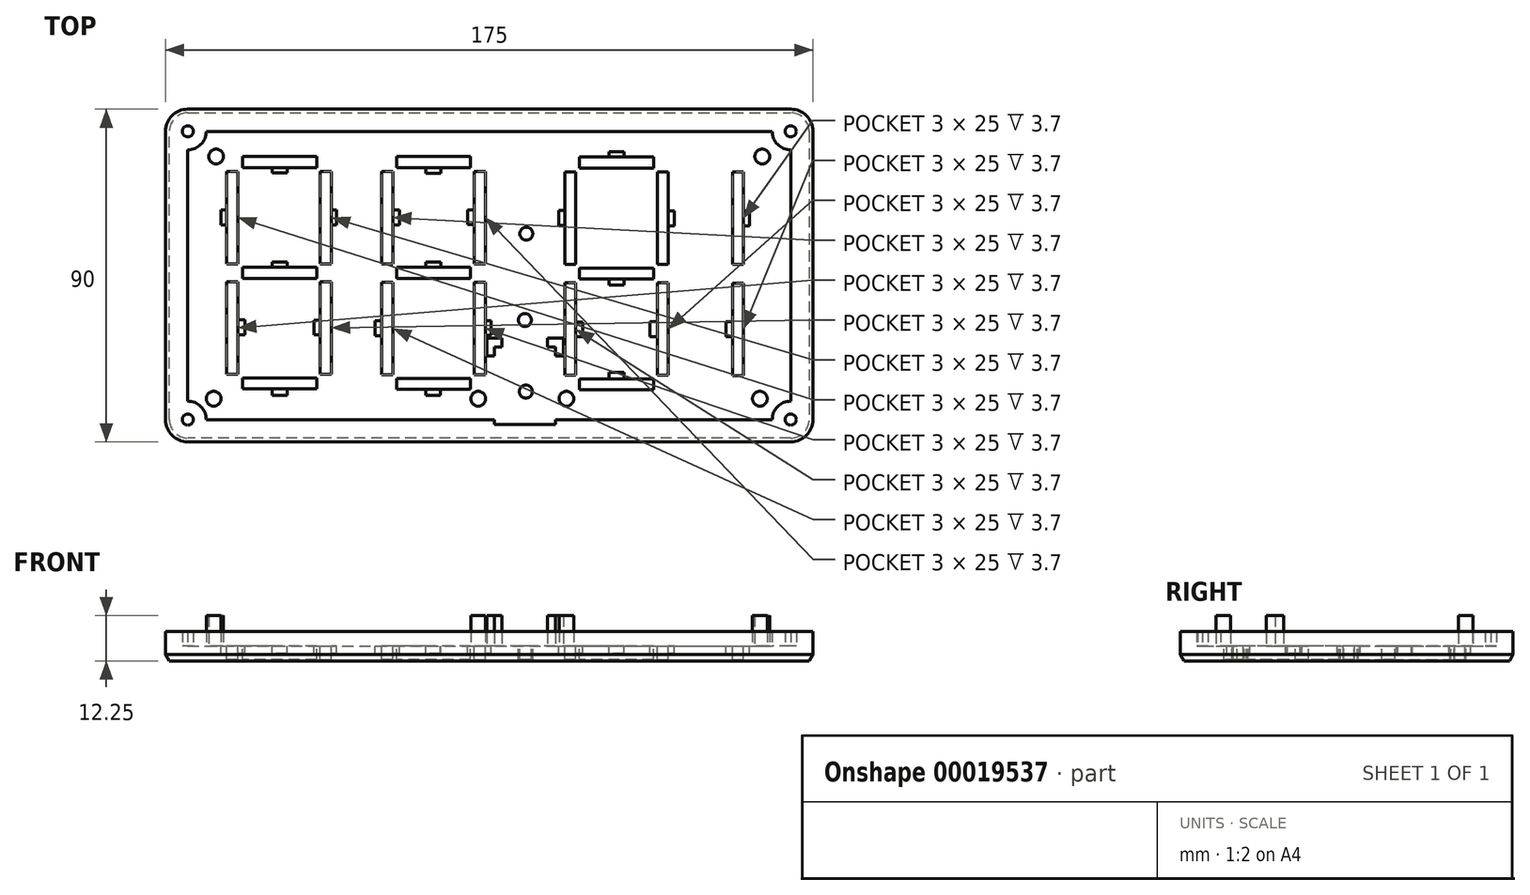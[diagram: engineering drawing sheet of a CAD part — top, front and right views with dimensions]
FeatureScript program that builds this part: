
annotation { "Feature Type Name" : "Feature", "Feature Type Description" : "" }
export const myFeature = defineFeature(function(context is Context, id is Id, definition is map)
    precondition{}
    {
        {
            var Q0;
            Q0=qCreatedBy(makeId("Top.planeOp"),FACE);
            var sketch = newSketch(context, id + "F0", { "sketchPlane" : qUnion([Q0])});
            skLineSegment(sketch, "E0.bottom", {"start": v(-87.5, 45) * mm, "end": v(87.5, 45) * mm});
            skLineSegment(sketch, "E0.top", {"start": v(-87.5, -45) * mm, "end": v(87.5, -45) * mm});
            skLineSegment(sketch, "E0.left", {"start": v(-87.5, 45) * mm, "end": v(-87.5, -45) * mm});
            skLineSegment(sketch, "E0.right", {"start": v(87.5, 45) * mm, "end": v(87.5, -45) * mm});
            skArc(sketch, "E1", {"start": v(-81.5, 34) * mm, "mid": v(-77.96, 35.46) * mm, "end": v(-76.5, 39) * mm});
            skArc(sketch, "E2", {"start": v(76.5, 39) * mm, "mid": v(77.96, 35.46) * mm, "end": v(81.5, 34) * mm});
            skArc(sketch, "E3", {"start": v(-76.5, -39) * mm, "mid": v(-77.96, -35.46) * mm, "end": v(-81.5, -34) * mm});
            skArc(sketch, "E4", {"start": v(81.5, -34) * mm, "mid": v(77.96, -35.46) * mm, "end": v(76.5, -39) * mm});
            skLineSegment(sketch, "E5", {"start": v(0, 39) * mm, "end": v(0, 0) * mm, "construction": true});
            skLineSegment(sketch, "E6.top", {"start": v(-68.01, -26.67) * mm, "end": v(-71.01, -26.67) * mm});
            skLineSegment(sketch, "E6.left", {"start": v(-68.01, -1.67) * mm, "end": v(-68.01, -26.67) * mm});
            skLineSegment(sketch, "E7.left", {"start": v(-68.01, 3.19) * mm, "end": v(-68.01, 28.19) * mm});
            skLineSegment(sketch, "E6.right", {"start": v(-71.01, -1.67) * mm, "end": v(-71.01, -26.67) * mm});
            skLineSegment(sketch, "E7.right", {"start": v(-71.01, 3.19) * mm, "end": v(-71.01, 28.19) * mm});
            skLineSegment(sketch, "E8.bottom", {"start": v(-45.68, -1.67) * mm, "end": v(-42.68, -1.67) * mm});
            skLineSegment(sketch, "E8.top", {"start": v(-45.68, -26.67) * mm, "end": v(-42.68, -26.67) * mm});
            skLineSegment(sketch, "E9.left", {"start": v(-46.68, 2.19) * mm, "end": v(-46.68, 29.19) * mm, "construction": true});
            skLineSegment(sketch, "E8.left", {"start": v(-45.68, -1.67) * mm, "end": v(-45.68, -26.67) * mm});
            skLineSegment(sketch, "E8.right", {"start": v(-42.68, -1.67) * mm, "end": v(-42.68, -26.67) * mm});
            skLineSegment(sketch, "E9.right", {"start": v(-41.68, 2.19) * mm, "end": v(-41.68, 29.19) * mm, "construction": true});
            skLineSegment(sketch, "E10", {"start": v(-45.68, -26.67) * mm, "end": v(-68.01, -26.67) * mm, "construction": true});
            skLineSegment(sketch, "E11.bottom", {"start": v(-46.68, -27.67) * mm, "end": v(-66.68, -27.67) * mm});
            skLineSegment(sketch, "E11.top", {"start": v(-46.68, -30.67) * mm, "end": v(-66.68, -30.67) * mm});
            skLineSegment(sketch, "E12.left", {"start": v(-66.68, 2.19) * mm, "end": v(-66.68, 29.19) * mm, "construction": true});
            skLineSegment(sketch, "E12.right", {"start": v(-72.01, 2.19) * mm, "end": v(-72.01, 29.19) * mm, "construction": true});
            skLineSegment(sketch, "E13.bottom", {"start": v(-46.68, 29.19) * mm, "end": v(-66.68, 29.19) * mm});
            skLineSegment(sketch, "E13.top", {"start": v(-46.68, 32.19) * mm, "end": v(-66.68, 32.19) * mm});
            skLineSegment(sketch, "E14.right", {"start": v(-42.68, 3.19) * mm, "end": v(-42.68, 28.19) * mm});
            skLineSegment(sketch, "E15.rect.bottom", {"start": v(-46.68, 2.19) * mm, "end": v(-66.68, 2.19) * mm});
            skLineSegment(sketch, "E15.rect.top", {"start": v(-46.68, -0.81) * mm, "end": v(-66.68, -0.81) * mm});
            skLineSegment(sketch, "E16.rect.bottom", {"start": v(-45.68, 3.19) * mm, "end": v(-68.01, 3.19) * mm, "construction": true});
            skLineSegment(sketch, "E16.rect.top", {"start": v(-45.68, -1.67) * mm, "end": v(-68.01, -1.67) * mm, "construction": true});
            skLineSegment(sketch, "E14.bottom", {"start": v(-45.68, 3.19) * mm, "end": v(-42.68, 3.19) * mm});
            skLineSegment(sketch, "E14.left", {"start": v(-45.68, 3.19) * mm, "end": v(-45.68, 28.19) * mm});
            skLineSegment(sketch, "E9.top", {"start": v(-46.68, 29.19) * mm, "end": v(-41.68, 29.19) * mm, "construction": true});
            skLineSegment(sketch, "E12.bottom", {"start": v(-66.68, 2.19) * mm, "end": v(-72.01, 2.19) * mm, "construction": true});
            skLineSegment(sketch, "E12.top", {"start": v(-66.68, 29.19) * mm, "end": v(-72.01, 29.19) * mm, "construction": true});
            skLineSegment(sketch, "E11.left", {"start": v(-46.68, -27.67) * mm, "end": v(-46.68, -30.67) * mm});
            skLineSegment(sketch, "E11.right", {"start": v(-66.68, -27.67) * mm, "end": v(-66.68, -30.67) * mm});
            skLineSegment(sketch, "E13.right", {"start": v(-66.68, 29.19) * mm, "end": v(-66.68, 32.19) * mm});
            skLineSegment(sketch, "E7.bottom", {"start": v(-68.01, 3.19) * mm, "end": v(-71.01, 3.19) * mm});
            skLineSegment(sketch, "E7.top", {"start": v(-68.01, 28.19) * mm, "end": v(-71.01, 28.19) * mm});
            skLineSegment(sketch, "E15.rect.left", {"start": v(-46.68, 2.19) * mm, "end": v(-46.68, -0.81) * mm});
            skLineSegment(sketch, "E15.rect.right", {"start": v(-66.68, 2.19) * mm, "end": v(-66.68, -0.81) * mm});
            skLineSegment(sketch, "E16.rect.right", {"start": v(-68.01, 3.19) * mm, "end": v(-68.01, -1.67) * mm, "construction": true});
            skLineSegment(sketch, "E13.left", {"start": v(-46.68, 29.19) * mm, "end": v(-46.68, 32.19) * mm});
            skLineSegment(sketch, "E14.top", {"start": v(-45.68, 28.19) * mm, "end": v(-42.68, 28.19) * mm});
            skLineSegment(sketch, "E6.bottom", {"start": v(-68.01, -1.67) * mm, "end": v(-71.01, -1.67) * mm});
            skLineSegment(sketch, "E9.bottom", {"start": v(-46.68, 2.19) * mm, "end": v(-41.68, 2.19) * mm, "construction": true});
            skLineSegment(sketch, "E16.rect.left", {"start": v(-45.68, 3.19) * mm, "end": v(-45.68, -1.67) * mm, "construction": true});
            skLineSegment(sketch, "E17.1.0.5", {"start": v(-5.06, -27.81) * mm, "end": v(-25.06, -27.81) * mm});
            skLineSegment(sketch, "E17.1.0.7", {"start": v(-4.06, -1.81) * mm, "end": v(-1.06, -1.81) * mm});
            skLineSegment(sketch, "E17.1.0.12", {"start": v(-4.06, 28.19) * mm, "end": v(-1.06, 28.19) * mm});
            skLineSegment(sketch, "E17.1.0.14", {"start": v(-4.06, 3.19) * mm, "end": v(-26.06, 3.19) * mm, "construction": true});
            skLineSegment(sketch, "E17.1.0.15", {"start": v(-26.06, -1.81) * mm, "end": v(-26.06, -26.81) * mm});
            skLineSegment(sketch, "E17.1.0.28", {"start": v(-5.06, -30.81) * mm, "end": v(-25.06, -30.81) * mm});
            skLineSegment(sketch, "E17.1.0.29", {"start": v(-1.06, -1.81) * mm, "end": v(-1.06, -26.81) * mm});
            skLineSegment(sketch, "E17.1.0.31", {"start": v(-4.06, -26.81) * mm, "end": v(-1.06, -26.81) * mm});
            skLineSegment(sketch, "E17.1.0.34", {"start": v(-26.06, 28.19) * mm, "end": v(-29.06, 28.19) * mm});
            skLineSegment(sketch, "E17.1.0.35", {"start": v(-5.06, 29.19) * mm, "end": v(-25.06, 29.19) * mm});
            skLineSegment(sketch, "E17.1.0.36", {"start": v(-29.06, -1.81) * mm, "end": v(-29.06, -26.81) * mm});
            skLineSegment(sketch, "E17.1.0.38", {"start": v(-5.06, 2.19) * mm, "end": v(-25.06, 2.19) * mm});
            skLineSegment(sketch, "E17.1.0.39", {"start": v(-26.06, -1.81) * mm, "end": v(-29.06, -1.81) * mm});
            skLineSegment(sketch, "E17.1.0.50", {"start": v(-4.06, -26.81) * mm, "end": v(-26.06, -26.81) * mm, "construction": true});
            skLineSegment(sketch, "E17.1.0.51", {"start": v(-4.06, -1.81) * mm, "end": v(-4.06, -26.81) * mm});
            skLineSegment(sketch, "E17.1.0.52", {"start": v(-5.06, 2.19) * mm, "end": v(-5.06, -0.81) * mm});
            skLineSegment(sketch, "E17.1.0.53", {"start": v(-4.06, 3.19) * mm, "end": v(-4.06, 28.19) * mm});
            skLineSegment(sketch, "E17.1.0.54", {"start": v(-5.06, 32.19) * mm, "end": v(-25.06, 32.19) * mm});
            skLineSegment(sketch, "E17.1.0.55", {"start": v(-29.06, 3.19) * mm, "end": v(-29.06, 28.19) * mm});
            skLineSegment(sketch, "E17.1.0.57", {"start": v(-30.06, 2.19) * mm, "end": v(-30.06, 29.19) * mm, "construction": true});
            skLineSegment(sketch, "E17.1.0.58", {"start": v(-4.06, -1.81) * mm, "end": v(-26.06, -1.81) * mm, "construction": true});
            skLineSegment(sketch, "E17.1.0.61", {"start": v(-26.06, 3.19) * mm, "end": v(-26.06, 28.19) * mm});
            skLineSegment(sketch, "E17.1.0.65", {"start": v(-25.06, 2.19) * mm, "end": v(-25.06, -0.81) * mm});
            skLineSegment(sketch, "E17.1.0.67", {"start": v(-1.06, 3.19) * mm, "end": v(-1.06, 28.19) * mm});
            skLineSegment(sketch, "E17.1.0.76", {"start": v(-25.06, 2.19) * mm, "end": v(-25.06, 29.19) * mm, "construction": true});
            skLineSegment(sketch, "E17.1.0.77", {"start": v(-5.06, -0.81) * mm, "end": v(-25.06, -0.81) * mm});
            skLineSegment(sketch, "E17.1.0.78", {"start": v(-0.06, 2.19) * mm, "end": v(-0.06, 29.19) * mm, "construction": true});
            skLineSegment(sketch, "E17.1.0.80", {"start": v(-5.06, 2.19) * mm, "end": v(-5.06, 29.19) * mm, "construction": true});
            skLineSegment(sketch, "E17.1.0.82", {"start": v(-5.06, -27.81) * mm, "end": v(-5.06, -30.81) * mm});
            skLineSegment(sketch, "E17.1.0.83", {"start": v(-26.06, -26.81) * mm, "end": v(-29.06, -26.81) * mm});
            skLineSegment(sketch, "E17.1.0.88", {"start": v(-5.06, 29.19) * mm, "end": v(-5.06, 32.19) * mm});
            skLineSegment(sketch, "E17.1.0.90", {"start": v(-25.06, -27.81) * mm, "end": v(-25.06, -30.81) * mm});
            skLineSegment(sketch, "E17.1.0.91", {"start": v(-5.06, 29.19) * mm, "end": v(-0.06, 29.19) * mm, "construction": true});
            skLineSegment(sketch, "E17.1.0.94", {"start": v(-5.06, 2.19) * mm, "end": v(-0.06, 2.19) * mm, "construction": true});
            skLineSegment(sketch, "E17.1.0.96", {"start": v(-4.06, 3.19) * mm, "end": v(-1.06, 3.19) * mm});
            skLineSegment(sketch, "E17.1.0.99", {"start": v(-26.06, 3.19) * mm, "end": v(-26.06, -1.81) * mm, "construction": true});
            skLineSegment(sketch, "E17.1.0.103", {"start": v(-26.06, 3.19) * mm, "end": v(-29.06, 3.19) * mm});
            skLineSegment(sketch, "E17.1.0.104", {"start": v(-25.06, 29.19) * mm, "end": v(-30.06, 29.19) * mm, "construction": true});
            skLineSegment(sketch, "E17.1.0.110", {"start": v(-25.06, 29.19) * mm, "end": v(-25.06, 32.19) * mm});
            skLineSegment(sketch, "E17.1.0.111", {"start": v(-25.06, 2.19) * mm, "end": v(-30.06, 2.19) * mm, "construction": true});
            skLineSegment(sketch, "E17.1.0.115", {"start": v(-4.06, 3.19) * mm, "end": v(-4.06, -1.81) * mm, "construction": true});
            skLineSegment(sketch, "E17.direction1", {"start": v(-42.68, 3.19) * mm, "end": v(-7.01, 3.19) * mm, "construction": true});
            skLineSegment(sketch, "E18.1.0.5", {"start": v(44.4, -27.96) * mm, "end": v(24.4, -27.96) * mm});
            skLineSegment(sketch, "E18.1.0.28", {"start": v(44.4, -30.96) * mm, "end": v(24.4, -30.96) * mm});
            skLineSegment(sketch, "E18.1.0.61", {"start": v(23.4, 3.04) * mm, "end": v(23.4, 28.04) * mm});
            skLineSegment(sketch, "E18.1.0.78", {"start": v(49.4, 2.04) * mm, "end": v(49.4, 29.04) * mm, "construction": true});
            skLineSegment(sketch, "E18.1.0.54", {"start": v(44.4, 32.04) * mm, "end": v(24.4, 32.04) * mm});
            skLineSegment(sketch, "E18.1.0.36", {"start": v(20.4, -1.96) * mm, "end": v(20.4, -26.96) * mm});
            skLineSegment(sketch, "E18.1.0.38", {"start": v(44.4, 2.04) * mm, "end": v(24.4, 2.04) * mm});
            skLineSegment(sketch, "E18.1.0.35", {"start": v(44.4, 29.04) * mm, "end": v(24.4, 29.04) * mm});
            skLineSegment(sketch, "E18.1.0.77", {"start": v(44.4, -0.96) * mm, "end": v(24.4, -0.96) * mm});
            skLineSegment(sketch, "E18.1.0.55", {"start": v(20.4, 3.04) * mm, "end": v(20.4, 28.04) * mm});
            skLineSegment(sketch, "E18.1.0.57", {"start": v(19.4, 2.04) * mm, "end": v(19.4, 29.04) * mm, "construction": true});
            skLineSegment(sketch, "E18.1.0.80", {"start": v(44.4, 2.04) * mm, "end": v(44.4, 29.04) * mm, "construction": true});
            skLineSegment(sketch, "E18.1.0.53", {"start": v(45.4, 3.04) * mm, "end": v(45.4, 28.04) * mm});
            skLineSegment(sketch, "E18.1.0.51", {"start": v(45.4, -1.96) * mm, "end": v(45.4, -26.96) * mm});
            skLineSegment(sketch, "E18.1.0.29", {"start": v(48.4, -1.96) * mm, "end": v(48.4, -26.96) * mm});
            skLineSegment(sketch, "E18.1.0.76", {"start": v(24.4, 2.04) * mm, "end": v(24.4, 29.04) * mm, "construction": true});
            skLineSegment(sketch, "E18.1.0.67", {"start": v(48.4, 3.04) * mm, "end": v(48.4, 28.04) * mm});
            skLineSegment(sketch, "E18.1.0.50", {"start": v(45.4, -26.96) * mm, "end": v(23.4, -26.96) * mm, "construction": true});
            skLineSegment(sketch, "E18.1.0.58", {"start": v(45.4, -1.96) * mm, "end": v(23.4, -1.96) * mm, "construction": true});
            skLineSegment(sketch, "E18.1.0.15", {"start": v(23.4, -1.96) * mm, "end": v(23.4, -26.96) * mm});
            skLineSegment(sketch, "E18.1.0.14", {"start": v(45.4, 3.04) * mm, "end": v(23.4, 3.04) * mm, "construction": true});
            skLineSegment(sketch, "E18.1.0.12", {"start": v(45.4, 28.04) * mm, "end": v(48.4, 28.04) * mm});
            skLineSegment(sketch, "E18.1.0.91", {"start": v(44.4, 29.04) * mm, "end": v(49.4, 29.04) * mm, "construction": true});
            skLineSegment(sketch, "E18.1.0.90", {"start": v(24.4, -27.96) * mm, "end": v(24.4, -30.96) * mm});
            skLineSegment(sketch, "E18.1.0.111", {"start": v(24.4, 2.04) * mm, "end": v(19.4, 2.04) * mm, "construction": true});
            skLineSegment(sketch, "E18.1.0.34", {"start": v(23.4, 28.04) * mm, "end": v(20.4, 28.04) * mm});
            skLineSegment(sketch, "E18.1.0.104", {"start": v(24.4, 29.04) * mm, "end": v(19.4, 29.04) * mm, "construction": true});
            skLineSegment(sketch, "E18.1.0.82", {"start": v(44.4, -27.96) * mm, "end": v(44.4, -30.96) * mm});
            skLineSegment(sketch, "E18.1.0.94", {"start": v(44.4, 2.04) * mm, "end": v(49.4, 2.04) * mm, "construction": true});
            skLineSegment(sketch, "E18.1.0.31", {"start": v(45.4, -26.96) * mm, "end": v(48.4, -26.96) * mm});
            skLineSegment(sketch, "E18.1.0.83", {"start": v(23.4, -26.96) * mm, "end": v(20.4, -26.96) * mm});
            skLineSegment(sketch, "E18.1.0.88", {"start": v(44.4, 29.04) * mm, "end": v(44.4, 32.04) * mm});
            skLineSegment(sketch, "E18.1.0.96", {"start": v(45.4, 3.04) * mm, "end": v(48.4, 3.04) * mm});
            skLineSegment(sketch, "E18.1.0.103", {"start": v(23.4, 3.04) * mm, "end": v(20.4, 3.04) * mm});
            skLineSegment(sketch, "E18.1.0.99", {"start": v(23.4, 3.04) * mm, "end": v(23.4, -1.96) * mm, "construction": true});
            skLineSegment(sketch, "E18.1.0.7", {"start": v(45.4, -1.96) * mm, "end": v(48.4, -1.96) * mm});
            skLineSegment(sketch, "E18.1.0.115", {"start": v(45.4, 3.04) * mm, "end": v(45.4, -1.96) * mm, "construction": true});
            skLineSegment(sketch, "E18.1.0.52", {"start": v(44.4, 2.04) * mm, "end": v(44.4, -0.96) * mm});
            skLineSegment(sketch, "E18.1.0.110", {"start": v(24.4, 29.04) * mm, "end": v(24.4, 32.04) * mm});
            skLineSegment(sketch, "E18.1.0.65", {"start": v(24.4, 2.04) * mm, "end": v(24.4, -0.96) * mm});
            skLineSegment(sketch, "E18.1.0.39", {"start": v(23.4, -1.96) * mm, "end": v(20.4, -1.96) * mm});
            skLineSegment(sketch, "E19.1.0.51", {"start": v(65.76, -2.04) * mm, "end": v(65.76, -27.04) * mm});
            skLineSegment(sketch, "E19.1.0.29", {"start": v(68.76, -2.04) * mm, "end": v(68.76, -27.04) * mm});
            skLineSegment(sketch, "E19.1.0.53", {"start": v(65.76, 2.96) * mm, "end": v(65.76, 27.96) * mm});
            skLineSegment(sketch, "E19.1.0.78", {"start": v(69.76, 1.96) * mm, "end": v(69.76, 28.96) * mm, "construction": true});
            skLineSegment(sketch, "E19.1.0.67", {"start": v(68.76, 2.96) * mm, "end": v(68.76, 27.96) * mm});
            skLineSegment(sketch, "E19.1.0.80", {"start": v(64.76, 1.96) * mm, "end": v(64.76, 28.96) * mm, "construction": true});
            skLineSegment(sketch, "E19.1.0.31", {"start": v(65.76, -27.04) * mm, "end": v(68.76, -27.04) * mm});
            skLineSegment(sketch, "E19.1.0.96", {"start": v(65.76, 2.96) * mm, "end": v(68.76, 2.96) * mm});
            skLineSegment(sketch, "E19.1.0.12", {"start": v(65.76, 27.96) * mm, "end": v(68.76, 27.96) * mm});
            skLineSegment(sketch, "E19.1.0.94", {"start": v(64.76, 1.96) * mm, "end": v(69.76, 1.96) * mm, "construction": true});
            skLineSegment(sketch, "E19.1.0.7", {"start": v(65.76, -2.04) * mm, "end": v(68.76, -2.04) * mm});
            skLineSegment(sketch, "E19.1.0.91", {"start": v(64.76, 28.96) * mm, "end": v(69.76, 28.96) * mm, "construction": true});
            skLineSegment(sketch, "E19.1.0.115", {"start": v(65.76, 2.96) * mm, "end": v(65.76, -2.04) * mm, "construction": true});
            skLineSegment(sketch, "E20", {"start": v(-66.68, 32.19) * mm, "end": v(77.46, 32.19) * mm, "construction": true});
            skLineSegment(sketch, "E21", {"start": v(50.1, 29.04) * mm, "end": v(77.85, 29.04) * mm, "construction": true});
            skCircle(sketch, "E22", {"center": v(9.63, -12.05) * mm, "radius": 1.75 * mm});
            skCircle(sketch, "E23", {"center": v(10.03, 11.32) * mm, "radius": 1.75 * mm});
            skCircle(sketch, "E24", {"center": v(-81.5, 39) * mm, "radius": 1.5 * mm});
            skCircle(sketch, "E25", {"center": v(-81.5, -39) * mm, "radius": 1.5 * mm});
            skCircle(sketch, "E26", {"center": v(81.5, -39) * mm, "radius": 1.5 * mm});
            skCircle(sketch, "E27", {"center": v(81.5, 39) * mm, "radius": 1.5 * mm});
            skLineSegment(sketch, "E28.trimOffspring", {"start": v(81.5, 34) * mm, "end": v(81.5, -34) * mm});
            skLineSegment(sketch, "E29.trimOffspring", {"start": v(-76.5, -39) * mm, "end": v(17.9, -39) * mm});
            skLineSegment(sketch, "E30.trimOffspring", {"start": v(-81.5, 34) * mm, "end": v(-81.5, -34) * mm});
            skLineSegment(sketch, "E31.trimOffspring", {"start": v(-76.5, 39) * mm, "end": v(76.5, 39) * mm});
            skLineSegment(sketch, "E32.rect.bottom", {"start": v(17.9, -40.3) * mm, "end": v(1.4, -40.3) * mm});
            skLineSegment(sketch, "E32.rect.top", {"start": v(17.9, -19.35) * mm, "end": v(15.73, -19.35) * mm});
            skLineSegment(sketch, "E32.rect.left", {"start": v(17.9, -40.3) * mm, "end": v(17.9, -39) * mm});
            skLineSegment(sketch, "E32.rect.right", {"start": v(1.4, -40.3) * mm, "end": v(1.4, -39) * mm});
            skPoint(sketch, "E32.rect.middle", {"position": v(9.65, -29.82) * mm});
            skCircle(sketch, "E33", {"center": v(9.9, -31.41) * mm, "radius": 1.75 * mm});
            skLineSegment(sketch, "E34.rect.bottom", {"start": v(17.9, -21.72) * mm, "end": v(20.08, -21.72) * mm});
            skLineSegment(sketch, "E34.rect.top", {"start": v(15.73, -16.98) * mm, "end": v(20.08, -16.98) * mm});
            skLineSegment(sketch, "E34.rect.left", {"start": v(15.73, -19.35) * mm, "end": v(15.73, -16.98) * mm});
            skLineSegment(sketch, "E34.rect.right", {"start": v(20.08, -21.72) * mm, "end": v(20.08, -16.98) * mm});
            skPoint(sketch, "E34.rect.middle", {"position": v(17.9, -19.35) * mm});
            skLineSegment(sketch, "E35.rect.bottom", {"start": v(1.4, -21.72) * mm, "end": v(-0.6, -21.72) * mm});
            skLineSegment(sketch, "E35.rect.top", {"start": v(3.4, -16.98) * mm, "end": v(-0.6, -16.98) * mm});
            skLineSegment(sketch, "E35.rect.left", {"start": v(3.4, -19.35) * mm, "end": v(3.4, -16.98) * mm});
            skLineSegment(sketch, "E35.rect.right", {"start": v(-0.6, -21.72) * mm, "end": v(-0.6, -16.98) * mm});
            skPoint(sketch, "E35.rect.middle", {"position": v(1.4, -19.35) * mm});
            skPoint(sketch, "E36.orphan", {"position": v(3.4, -21.72) * mm});
            skPoint(sketch, "E37.orphan", {"position": v(15.73, -21.72) * mm});
            skLineSegment(sketch, "E38", {"start": v(3.4, -19.35) * mm, "end": v(1.4, -19.35) * mm});
            skLineSegment(sketch, "E39", {"start": v(15.73, -19.35) * mm, "end": v(3.4, -19.35) * mm, "construction": true});
            skLineSegment(sketch, "E40", {"start": v(1.4, -21.72) * mm, "end": v(1.4, -19.35) * mm});
            skLineSegment(sketch, "E41", {"start": v(17.9, -21.72) * mm, "end": v(17.9, -19.35) * mm});
            skLineSegment(sketch, "E42", {"start": v(17.9, -39) * mm, "end": v(76.5, -39) * mm});
            skLineSegment(sketch, "E43", {"start": v(1.4, -39) * mm, "end": v(1.4, -21.72) * mm, "construction": true});
            skLineSegment(sketch, "E44", {"start": v(17.9, -39) * mm, "end": v(17.9, -21.72) * mm, "construction": true});
            skCircle(sketch, "E45", {"center": v(73.8, 32.19) * mm, "radius": 2 * mm});
            skCircle(sketch, "E46", {"center": v(73.15, -33.33) * mm, "radius": 2 * mm});
            skCircle(sketch, "E47", {"center": v(-73.84, 32.19) * mm, "radius": 2 * mm});
            skCircle(sketch, "E48", {"center": v(-74.5, -33.33) * mm, "radius": 2 * mm});
            skCircle(sketch, "E49", {"center": v(20.87, -33.33) * mm, "radius": 2 * mm});
            skCircle(sketch, "E50", {"center": v(-2.98, -33.33) * mm, "radius": 2 * mm});
            skLineSegment(sketch, "E51.rect.bottom", {"start": v(-66.1, -16.02) * mm, "end": v(-68.01, -16.02) * mm});
            skLineSegment(sketch, "E51.rect.top", {"start": v(-66.1, -12.02) * mm, "end": v(-68.01, -12.02) * mm});
            skLineSegment(sketch, "E51.rect.left", {"start": v(-66.1, -16.02) * mm, "end": v(-66.1, -12.02) * mm});
            skLineSegment(sketch, "E52.rect.bottom", {"start": v(-47.39, -16.1) * mm, "end": v(-45.68, -16.1) * mm});
            skLineSegment(sketch, "E52.rect.top", {"start": v(-47.39, -12.1) * mm, "end": v(-45.68, -12.1) * mm});
            skLineSegment(sketch, "E52.rect.left", {"start": v(-47.39, -16.1) * mm, "end": v(-47.39, -12.1) * mm});
            skLineSegment(sketch, "E53.rect.bottom", {"start": v(-58.68, -32.37) * mm, "end": v(-54.68, -32.37) * mm});
            skLineSegment(sketch, "E53.rect.left", {"start": v(-58.68, -32.37) * mm, "end": v(-58.68, -30.67) * mm});
            skLineSegment(sketch, "E53.rect.right", {"start": v(-54.68, -32.37) * mm, "end": v(-54.68, -30.67) * mm});
            skLineSegment(sketch, "E54.rect.bottom", {"start": v(-58.68, 3.68) * mm, "end": v(-54.68, 3.68) * mm});
            skLineSegment(sketch, "E54.rect.left", {"start": v(-58.68, 3.68) * mm, "end": v(-58.68, 2.19) * mm});
            skLineSegment(sketch, "E54.rect.right", {"start": v(-54.68, 3.68) * mm, "end": v(-54.68, 2.19) * mm});
            skLineSegment(sketch, "E55.rect.bottom", {"start": v(-72.53, 13.69) * mm, "end": v(-71.01, 13.69) * mm});
            skLineSegment(sketch, "E55.rect.top", {"start": v(-72.53, 17.69) * mm, "end": v(-71.01, 17.69) * mm});
            skLineSegment(sketch, "E55.rect.left", {"start": v(-72.53, 13.69) * mm, "end": v(-72.53, 17.69) * mm});
            skLineSegment(sketch, "E56.rect.bottom", {"start": v(-58.68, 27.77) * mm, "end": v(-54.68, 27.77) * mm});
            skLineSegment(sketch, "E56.rect.left", {"start": v(-58.68, 27.77) * mm, "end": v(-58.68, 29.19) * mm});
            skLineSegment(sketch, "E56.rect.right", {"start": v(-54.68, 27.77) * mm, "end": v(-54.68, 29.19) * mm});
            skLineSegment(sketch, "E57.rect.bottom", {"start": v(-41.3, 17.68) * mm, "end": v(-42.68, 17.68) * mm});
            skLineSegment(sketch, "E57.rect.top", {"start": v(-41.3, 13.68) * mm, "end": v(-42.68, 13.68) * mm});
            skLineSegment(sketch, "E57.rect.left", {"start": v(-41.3, 17.68) * mm, "end": v(-41.3, 13.68) * mm});
            skLineSegment(sketch, "E58.rect.bottom", {"start": v(-17.1, 27.61) * mm, "end": v(-13.1, 27.61) * mm});
            skLineSegment(sketch, "E58.rect.left", {"start": v(-17.1, 27.61) * mm, "end": v(-17.1, 29.19) * mm});
            skLineSegment(sketch, "E58.rect.right", {"start": v(-13.1, 27.61) * mm, "end": v(-13.1, 29.19) * mm});
            skLineSegment(sketch, "E59.rect.bottom", {"start": v(-24.23, 17.69) * mm, "end": v(-26.06, 17.69) * mm});
            skLineSegment(sketch, "E59.rect.top", {"start": v(-24.23, 13.69) * mm, "end": v(-26.06, 13.69) * mm});
            skLineSegment(sketch, "E59.rect.left", {"start": v(-24.23, 17.69) * mm, "end": v(-24.23, 13.69) * mm});
            skLineSegment(sketch, "E60.rect.bottom", {"start": v(-5.85, 13.78) * mm, "end": v(-4.06, 13.78) * mm});
            skLineSegment(sketch, "E60.rect.top", {"start": v(-5.85, 17.78) * mm, "end": v(-4.06, 17.78) * mm});
            skLineSegment(sketch, "E60.rect.left", {"start": v(-5.85, 13.78) * mm, "end": v(-5.85, 17.78) * mm});
            skLineSegment(sketch, "E61.rect.bottom", {"start": v(-17.1, 3.6) * mm, "end": v(-13.1, 3.6) * mm});
            skLineSegment(sketch, "E61.rect.left", {"start": v(-17.1, 3.6) * mm, "end": v(-17.1, 2.19) * mm});
            skLineSegment(sketch, "E61.rect.right", {"start": v(-13.1, 3.6) * mm, "end": v(-13.1, 2.19) * mm});
            skLineSegment(sketch, "E62.rect.bottom", {"start": v(-30.88, -12.29) * mm, "end": v(-29.06, -12.29) * mm});
            skLineSegment(sketch, "E62.rect.top", {"start": v(-30.88, -16.29) * mm, "end": v(-29.06, -16.29) * mm});
            skLineSegment(sketch, "E62.rect.left", {"start": v(-30.88, -12.29) * mm, "end": v(-30.88, -16.29) * mm});
            skLineSegment(sketch, "E63.rect.bottom", {"start": v(0.5, -12.23) * mm, "end": v(-1.06, -12.23) * mm});
            skLineSegment(sketch, "E63.rect.top", {"start": v(0.5, -16.23) * mm, "end": v(-1.06, -16.23) * mm});
            skLineSegment(sketch, "E63.rect.left", {"start": v(0.5, -12.23) * mm, "end": v(0.5, -16.23) * mm});
            skLineSegment(sketch, "E64.rect.bottom", {"start": v(-17.16, -32.42) * mm, "end": v(-13.16, -32.42) * mm});
            skLineSegment(sketch, "E64.rect.left", {"start": v(-17.16, -32.42) * mm, "end": v(-17.16, -30.81) * mm});
            skLineSegment(sketch, "E64.rect.right", {"start": v(-13.16, -32.42) * mm, "end": v(-13.16, -30.81) * mm});
            skLineSegment(sketch, "E65.rect.bottom", {"start": v(32.4, 33.52) * mm, "end": v(36.4, 33.52) * mm});
            skLineSegment(sketch, "E65.rect.left", {"start": v(32.4, 33.52) * mm, "end": v(32.4, 32.04) * mm});
            skLineSegment(sketch, "E65.rect.right", {"start": v(36.4, 33.52) * mm, "end": v(36.4, 32.04) * mm});
            skLineSegment(sketch, "E66.rect.bottom", {"start": v(18.75, 13.55) * mm, "end": v(20.4, 13.55) * mm});
            skLineSegment(sketch, "E66.rect.top", {"start": v(18.75, 17.55) * mm, "end": v(20.4, 17.55) * mm});
            skLineSegment(sketch, "E66.rect.left", {"start": v(18.75, 13.55) * mm, "end": v(18.75, 17.55) * mm});
            skLineSegment(sketch, "E67.rect.bottom", {"start": v(50, 17.48) * mm, "end": v(48.4, 17.48) * mm});
            skLineSegment(sketch, "E67.rect.top", {"start": v(50, 13.48) * mm, "end": v(48.4, 13.48) * mm});
            skLineSegment(sketch, "E67.rect.left", {"start": v(50, 17.48) * mm, "end": v(50, 13.48) * mm});
            skLineSegment(sketch, "E68.rect.bottom", {"start": v(32.38, -2.53) * mm, "end": v(36.38, -2.53) * mm});
            skLineSegment(sketch, "E68.rect.left", {"start": v(32.38, -2.53) * mm, "end": v(32.38, -0.96) * mm});
            skLineSegment(sketch, "E68.rect.right", {"start": v(36.38, -2.53) * mm, "end": v(36.38, -0.96) * mm});
            skLineSegment(sketch, "E69.rect.bottom", {"start": v(25.28, -12.57) * mm, "end": v(23.4, -12.57) * mm});
            skLineSegment(sketch, "E69.rect.top", {"start": v(25.28, -16.57) * mm, "end": v(23.4, -16.57) * mm});
            skLineSegment(sketch, "E69.rect.left", {"start": v(25.28, -12.57) * mm, "end": v(25.28, -16.57) * mm});
            skLineSegment(sketch, "E70.rect.bottom", {"start": v(43.49, -16.54) * mm, "end": v(45.4, -16.54) * mm});
            skLineSegment(sketch, "E70.rect.top", {"start": v(43.49, -12.54) * mm, "end": v(45.4, -12.54) * mm});
            skLineSegment(sketch, "E70.rect.left", {"start": v(43.49, -16.54) * mm, "end": v(43.49, -12.54) * mm});
            skLineSegment(sketch, "E71.rect.bottom", {"start": v(36.43, -26.21) * mm, "end": v(32.43, -26.21) * mm});
            skLineSegment(sketch, "E71.rect.left", {"start": v(36.43, -26.21) * mm, "end": v(36.43, -27.96) * mm});
            skLineSegment(sketch, "E71.rect.right", {"start": v(32.43, -26.21) * mm, "end": v(32.43, -27.96) * mm});
            skLineSegment(sketch, "E72.rect.bottom", {"start": v(68.76, 17.48) * mm, "end": v(70.36, 17.48) * mm});
            skLineSegment(sketch, "E72.rect.top", {"start": v(68.76, 13.45) * mm, "end": v(70.36, 13.45) * mm});
            skLineSegment(sketch, "E72.rect.right", {"start": v(70.36, 17.48) * mm, "end": v(70.36, 13.45) * mm});
            skLineSegment(sketch, "E73.rect.bottom", {"start": v(63.96, -12.54) * mm, "end": v(65.76, -12.54) * mm});
            skLineSegment(sketch, "E73.rect.top", {"start": v(63.96, -16.53) * mm, "end": v(65.76, -16.53) * mm});
            skLineSegment(sketch, "E73.rect.left", {"start": v(63.96, -12.54) * mm, "end": v(63.96, -16.53) * mm});
            skSolve(sketch);
        }
        {
            var Q0;
            Q0=makeQuery(id+"F0.imprint","IMPRINT",FACE,{"disambiguationData":[TD([[makeQuery(id+"F0.imprint","IMPRINT",EDGE,{"derivedFrom":sQuery(id+"F0.wireOp",EDGE,"E0.bottom")}),-1.0]])]});
            var Q1;
            Q1=makeQuery(id+"F0.imprint","IMPRINT",FACE,{"disambiguationData":[TD([[makeQuery(id+"F0.imprint","IMPRINT",EDGE,{"derivedFrom":sQuery(id+"F0.wireOp",EDGE,"E17.1.0.5")}),1.0]])]});
            var Q2;
            {var subQ7=sQuery(id+"F0.wireOp",EDGE,"E17.1.0.12");Q2=makeQuery(id+"F0.imprint","IMPRINT",FACE,{"disambiguationData":[TD([[makeQuery(id+"F0.imprint","IMPRINT",EDGE,{"derivedFrom":subQ7}),-1.0]])]});}
            var Q3;
            {var subQ7=sQuery(id+"F0.wireOp",EDGE,"E17.1.0.7");Q3=makeQuery(id+"F0.imprint","IMPRINT",FACE,{"disambiguationData":[TD([[makeQuery(id+"F0.imprint","IMPRINT",EDGE,{"derivedFrom":subQ7}),-1.0]])]});}
            var Q4;
            Q4=makeQuery(id+"F0.imprint","IMPRINT",FACE,{"disambiguationData":[TD([[makeQuery(id+"F0.imprint","IMPRINT",EDGE,{"derivedFrom":sQuery(id+"F0.wireOp",EDGE,"E11.bottom")}),1.0]])]});
            var Q5;
            Q5=makeQuery(id+"F0.imprint","IMPRINT",FACE,{"disambiguationData":[TD([[makeQuery(id+"F0.imprint","IMPRINT",EDGE,{"derivedFrom":sQuery(id+"F0.wireOp",EDGE,"E18.1.0.38")}),1.0]])]});
            var Q6;
            Q6=makeQuery(id+"F0.imprint","IMPRINT",FACE,{"disambiguationData":[TD([[makeQuery(id+"F0.imprint","IMPRINT",EDGE,{"derivedFrom":sQuery(id+"F0.wireOp",EDGE,"E18.1.0.29")}),-1.0]])]});
            var Q7;
            Q7=makeQuery(id+"F0.imprint","IMPRINT",FACE,{"disambiguationData":[TD([[makeQuery(id+"F0.imprint","IMPRINT",EDGE,{"derivedFrom":sQuery(id+"F0.wireOp",EDGE,"E18.1.0.28")}),-1.0]])]});
            var Q8;
            {var subQ7=sQuery(id+"F0.wireOp",EDGE,"E6.top");Q8=makeQuery(id+"F0.imprint","IMPRINT",FACE,{"disambiguationData":[TD([[makeQuery(id+"F0.imprint","IMPRINT",EDGE,{"derivedFrom":subQ7}),-1.0]])]});}
            var Q9;
            Q9=makeQuery(id+"F0.imprint","IMPRINT",FACE,{"disambiguationData":[TD([[makeQuery(id+"F0.imprint","IMPRINT",EDGE,{"derivedFrom":sQuery(id+"F0.wireOp",EDGE,"E7.left")}),1.0]])]});
            var Q10;
            {var subQ7=sQuery(id+"F0.wireOp",EDGE,"E8.bottom");Q10=makeQuery(id+"F0.imprint","IMPRINT",FACE,{"disambiguationData":[TD([[makeQuery(id+"F0.imprint","IMPRINT",EDGE,{"derivedFrom":subQ7}),-1.0]])]});}
            var Q11;
            Q11=makeQuery(id+"F0.imprint","IMPRINT",FACE,{"disambiguationData":[TD([[makeQuery(id+"F0.imprint","IMPRINT",EDGE,{"derivedFrom":sQuery(id+"F0.wireOp",EDGE,"E13.top")}),1.0]])]});
            var Q12;
            {var subQ7=sQuery(id+"F0.wireOp",EDGE,"E14.bottom");Q12=makeQuery(id+"F0.imprint","IMPRINT",FACE,{"disambiguationData":[TD([[makeQuery(id+"F0.imprint","IMPRINT",EDGE,{"derivedFrom":subQ7}),1.0]])]});}
            var Q13;
            Q13=makeQuery(id+"F0.imprint","IMPRINT",FACE,{"disambiguationData":[TD([[makeQuery(id+"F0.imprint","IMPRINT",EDGE,{"derivedFrom":sQuery(id+"F0.wireOp",EDGE,"E15.rect.top")}),-1.0]])]});
            var Q14;
            Q14=makeQuery(id+"F0.imprint","IMPRINT",FACE,{"disambiguationData":[TD([[makeQuery(id+"F0.imprint","IMPRINT",EDGE,{"derivedFrom":sQuery(id+"F0.wireOp",EDGE,"E19.1.0.53")}),-1.0]])]});
            var Q15;
            Q15=makeQuery(id+"F0.imprint","IMPRINT",FACE,{"disambiguationData":[TD([[makeQuery(id+"F0.imprint","IMPRINT",EDGE,{"derivedFrom":sQuery(id+"F0.wireOp",EDGE,"E18.1.0.61")}),1.0]])]});
            var Q16;
            {var subQ7=sQuery(id+"F0.wireOp",EDGE,"E17.1.0.52");Q16=makeQuery(id+"F0.imprint","IMPRINT",FACE,{"disambiguationData":[TD([[makeQuery(id+"F0.imprint","IMPRINT",EDGE,{"derivedFrom":subQ7}),-1.0]])]});}
            var Q17;
            Q17=makeQuery(id+"F0.imprint","IMPRINT",FACE,{"disambiguationData":[TD([[makeQuery(id+"F0.imprint","IMPRINT",EDGE,{"derivedFrom":sQuery(id+"F0.wireOp",EDGE,"E1")}),-1.0]])]});
            var Q18;
            Q18=makeQuery(id+"F0.imprint","IMPRINT",FACE,{"disambiguationData":[TD([[makeQuery(id+"F0.imprint","IMPRINT",EDGE,{"derivedFrom":sQuery(id+"F0.wireOp",EDGE,"E18.1.0.36")}),1.0]])]});
            var Q19;
            Q19=makeQuery(id+"F0.imprint","IMPRINT",FACE,{"disambiguationData":[TD([[makeQuery(id+"F0.imprint","IMPRINT",EDGE,{"derivedFrom":sQuery(id+"F0.wireOp",EDGE,"E17.1.0.54")}),1.0]])]});
            var Q20;
            Q20=makeQuery(id+"F0.imprint","IMPRINT",FACE,{"disambiguationData":[TD([[makeQuery(id+"F0.imprint","IMPRINT",EDGE,{"derivedFrom":sQuery(id+"F0.wireOp",EDGE,"E19.1.0.29")}),-1.0]])]});
            var Q21;
            Q21=makeQuery(id+"F0.imprint","IMPRINT",FACE,{"disambiguationData":[TD([[makeQuery(id+"F0.imprint","IMPRINT",EDGE,{"derivedFrom":sQuery(id+"F0.wireOp",EDGE,"E17.1.0.15")}),-1.0]])]});
            var Q22;
            {var subQ6=sQuery(id+"F0.wireOp",EDGE,"E17.1.0.34");Q22=makeQuery(id+"F0.imprint","IMPRINT",FACE,{"disambiguationData":[TD([[makeQuery(id+"F0.imprint","IMPRINT",EDGE,{"derivedFrom":subQ6}),1.0]])]});}
            var Q23;
            Q23=makeQuery(id+"F0.imprint","IMPRINT",FACE,{"disambiguationData":[TD([[makeQuery(id+"F0.imprint","IMPRINT",EDGE,{"derivedFrom":sQuery(id+"F0.wireOp",EDGE,"E18.1.0.53")}),-1.0]])]});
            var Q24;
            Q24=makeQuery(id+"F0.imprint","IMPRINT",FACE,{"disambiguationData":[TD([[makeQuery(id+"F0.imprint","IMPRINT",EDGE,{"derivedFrom":sQuery(id+"F0.wireOp",EDGE,"E18.1.0.35")}),-1.0]])]});
            var Q25;
            Q25=makeQuery(id+"F0.imprint","IMPRINT",FACE,{"disambiguationData":[TD([[makeQuery(id+"F0.imprint","IMPRINT",EDGE,{"derivedFrom":sQuery(id+"F0.wireOp",EDGE,"E22")}),1.0]])]});
            var Q26;
            Q26=makeQuery(id+"F0.imprint","IMPRINT",FACE,{"disambiguationData":[TD([[makeQuery(id+"F0.imprint","IMPRINT",EDGE,{"derivedFrom":sQuery(id+"F0.wireOp",EDGE,"E23")}),1.0]])]});
            var Q27;
            Q27=makeQuery(id+"F0.imprint","IMPRINT",FACE,{"disambiguationData":[TD([[makeQuery(id+"F0.imprint","IMPRINT",EDGE,{"derivedFrom":sQuery(id+"F0.wireOp",EDGE,"E24")}),1.0]])]});
            var Q28;
            Q28=makeQuery(id+"F0.imprint","IMPRINT",FACE,{"disambiguationData":[TD([[makeQuery(id+"F0.imprint","IMPRINT",EDGE,{"derivedFrom":sQuery(id+"F0.wireOp",EDGE,"E25")}),1.0]])]});
            var Q29;
            Q29=makeQuery(id+"F0.imprint","IMPRINT",FACE,{"disambiguationData":[TD([[makeQuery(id+"F0.imprint","IMPRINT",EDGE,{"derivedFrom":sQuery(id+"F0.wireOp",EDGE,"E26")}),1.0]])]});
            var Q30;
            Q30=makeQuery(id+"F0.imprint","IMPRINT",FACE,{"disambiguationData":[TD([[makeQuery(id+"F0.imprint","IMPRINT",EDGE,{"derivedFrom":sQuery(id+"F0.wireOp",EDGE,"E27")}),1.0]])]});
            var Q31;
            {var subQ3=sQuery(id+"F0.wireOp",EDGE,"d27d8e91-9dc8-4657-a3bc-17c214d1fbd1.rect.top");Q31=makeQuery(id+"F0.imprint","IMPRINT",FACE,{"disambiguationData":[TD([[makeQuery(id+"F0.imprint","IMPRINT",EDGE,{"derivedFrom":subQ3}),1.0]])]});}
            var Q32;
            {var subQ3=sQuery(id+"F0.wireOp",EDGE,"d27d8e91-9dc8-4657-a3bc-17c214d1fbd1.rect.bottom");Q32=makeQuery(id+"F0.imprint","IMPRINT",FACE,{"disambiguationData":[TD([[makeQuery(id+"F0.imprint","IMPRINT",EDGE,{"derivedFrom":subQ3}),-1.0]])]});}
            var Q33;
            {var subQ0=sQuery(id+"F0.wireOp",EDGE,"11542846-51ec-4e1d-9889-e9b2482069cd.rect.left");Q33=makeQuery(id+"F0.imprint","IMPRINT",FACE,{"disambiguationData":[TD([[makeQuery(id+"F0.imprint","IMPRINT",EDGE,{"derivedFrom":subQ0}),-1.0]])]});}
            var Q34;
            {var subQ0=sQuery(id+"F0.wireOp",EDGE,"11542846-51ec-4e1d-9889-e9b2482069cd.rect.right");Q34=makeQuery(id+"F0.imprint","IMPRINT",FACE,{"disambiguationData":[TD([[makeQuery(id+"F0.imprint","IMPRINT",EDGE,{"derivedFrom":subQ0}),1.0]])]});}
            var Q35;
            {var subQ0=sQuery(id+"F0.wireOp",EDGE,"7a176b9b-9b07-41be-aea8-fdd94f8c28c8.rect.right");Q35=makeQuery(id+"F0.imprint","IMPRINT",FACE,{"disambiguationData":[TD([[makeQuery(id+"F0.imprint","IMPRINT",EDGE,{"derivedFrom":subQ0}),1.0]])]});}
            var Q36;
            {var subQ0=sQuery(id+"F0.wireOp",EDGE,"7a176b9b-9b07-41be-aea8-fdd94f8c28c8.rect.left");Q36=makeQuery(id+"F0.imprint","IMPRINT",FACE,{"disambiguationData":[TD([[makeQuery(id+"F0.imprint","IMPRINT",EDGE,{"derivedFrom":subQ0}),-1.0]])]});}
            var Q37;
            {var subQ0=sQuery(id+"F0.wireOp",EDGE,"7fec9149-b94b-4e31-a2bc-72143b81982d.rect.right");Q37=makeQuery(id+"F0.imprint","IMPRINT",FACE,{"disambiguationData":[TD([[makeQuery(id+"F0.imprint","IMPRINT",EDGE,{"derivedFrom":subQ0}),-1.0]])]});}
            var Q38;
            {var subQ0=sQuery(id+"F0.wireOp",EDGE,"7fec9149-b94b-4e31-a2bc-72143b81982d.rect.left");Q38=makeQuery(id+"F0.imprint","IMPRINT",FACE,{"disambiguationData":[TD([[makeQuery(id+"F0.imprint","IMPRINT",EDGE,{"derivedFrom":subQ0}),1.0]])]});}
            var Q39;
            {var subQ3=sQuery(id+"F0.wireOp",EDGE,"2390580b-736b-4805-a3aa-b3ade61d923c.rect.bottom");Q39=makeQuery(id+"F0.imprint","IMPRINT",FACE,{"disambiguationData":[TD([[makeQuery(id+"F0.imprint","IMPRINT",EDGE,{"derivedFrom":subQ3}),1.0]])]});}
            var Q40;
            {var subQ3=sQuery(id+"F0.wireOp",EDGE,"2390580b-736b-4805-a3aa-b3ade61d923c.rect.top");Q40=makeQuery(id+"F0.imprint","IMPRINT",FACE,{"disambiguationData":[TD([[makeQuery(id+"F0.imprint","IMPRINT",EDGE,{"derivedFrom":subQ3}),-1.0]])]});}
            var Q41;
            {var subQ0=sQuery(id+"F0.wireOp",EDGE,"2166e6f4-a4c2-4c34-8466-9477065b0f98.rect.left");Q41=makeQuery(id+"F0.imprint","IMPRINT",FACE,{"disambiguationData":[TD([[makeQuery(id+"F0.imprint","IMPRINT",EDGE,{"derivedFrom":subQ0}),1.0]])]});}
            var Q42;
            {var subQ0=sQuery(id+"F0.wireOp",EDGE,"2166e6f4-a4c2-4c34-8466-9477065b0f98.rect.right");Q42=makeQuery(id+"F0.imprint","IMPRINT",FACE,{"disambiguationData":[TD([[makeQuery(id+"F0.imprint","IMPRINT",EDGE,{"derivedFrom":subQ0}),-1.0]])]});}
            var Q43;
            {var subQ3=sQuery(id+"F0.wireOp",EDGE,"a0b229e6-3aa1-4465-9a5a-0985d3e63f01.rect.top");Q43=makeQuery(id+"F0.imprint","IMPRINT",FACE,{"disambiguationData":[TD([[makeQuery(id+"F0.imprint","IMPRINT",EDGE,{"derivedFrom":subQ3}),-1.0]])]});}
            var Q44;
            {var subQ0=sQuery(id+"F0.wireOp",EDGE,"1c78e4fe-e1cb-4ebb-b1fd-c2c0064fb7eb.rect.right");Q44=makeQuery(id+"F0.imprint","IMPRINT",FACE,{"disambiguationData":[TD([[makeQuery(id+"F0.imprint","IMPRINT",EDGE,{"derivedFrom":subQ0}),-1.0]])]});}
            var Q45;
            {var subQ3=sQuery(id+"F0.wireOp",EDGE,"6cf41ee3-29a7-4b54-a486-07bb11f7813b.rect.top");Q45=makeQuery(id+"F0.imprint","IMPRINT",FACE,{"disambiguationData":[TD([[makeQuery(id+"F0.imprint","IMPRINT",EDGE,{"derivedFrom":subQ3}),-1.0]])]});}
            var Q46;
            {var subQ0=sQuery(id+"F0.wireOp",EDGE,"892f925b-46cd-4a3b-8f99-ca5bc6e0e537.rect.right");Q46=makeQuery(id+"F0.imprint","IMPRINT",FACE,{"disambiguationData":[TD([[makeQuery(id+"F0.imprint","IMPRINT",EDGE,{"derivedFrom":subQ0}),1.0]])]});}
            var Q47;
            {var subQ3=sQuery(id+"F0.wireOp",EDGE,"6cf41ee3-29a7-4b54-a486-07bb11f7813b.rect.bottom");Q47=makeQuery(id+"F0.imprint","IMPRINT",FACE,{"disambiguationData":[TD([[makeQuery(id+"F0.imprint","IMPRINT",EDGE,{"derivedFrom":subQ3}),1.0]])]});}
            var Q48;
            {var subQ0=sQuery(id+"F0.wireOp",EDGE,"892f925b-46cd-4a3b-8f99-ca5bc6e0e537.rect.left");Q48=makeQuery(id+"F0.imprint","IMPRINT",FACE,{"disambiguationData":[TD([[makeQuery(id+"F0.imprint","IMPRINT",EDGE,{"derivedFrom":subQ0}),-1.0]])]});}
            var Q49;
            {var subQ3=sQuery(id+"F0.wireOp",EDGE,"a0b229e6-3aa1-4465-9a5a-0985d3e63f01.rect.bottom");Q49=makeQuery(id+"F0.imprint","IMPRINT",FACE,{"disambiguationData":[TD([[makeQuery(id+"F0.imprint","IMPRINT",EDGE,{"derivedFrom":subQ3}),1.0]])]});}
            var Q50;
            {var subQ0=sQuery(id+"F0.wireOp",EDGE,"1c78e4fe-e1cb-4ebb-b1fd-c2c0064fb7eb.rect.left");Q50=makeQuery(id+"F0.imprint","IMPRINT",FACE,{"disambiguationData":[TD([[makeQuery(id+"F0.imprint","IMPRINT",EDGE,{"derivedFrom":subQ0}),1.0]])]});}
            var Q51;
            {var subQ3=sQuery(id+"F0.wireOp",EDGE,"f48832b2-2d0e-43cf-9fc1-d9ed1891b05c.rect.top");Q51=makeQuery(id+"F0.imprint","IMPRINT",FACE,{"disambiguationData":[TD([[makeQuery(id+"F0.imprint","IMPRINT",EDGE,{"derivedFrom":subQ3}),-1.0]])]});}
            var Q52;
            {var subQ3=sQuery(id+"F0.wireOp",EDGE,"f48832b2-2d0e-43cf-9fc1-d9ed1891b05c.rect.bottom");Q52=makeQuery(id+"F0.imprint","IMPRINT",FACE,{"disambiguationData":[TD([[makeQuery(id+"F0.imprint","IMPRINT",EDGE,{"derivedFrom":subQ3}),1.0]])]});}
            var Q53;
            {var subQ0=sQuery(id+"F0.wireOp",EDGE,"1b435d11-bbf8-4d76-92a6-f0dfc75fd8fa.rect.left");Q53=makeQuery(id+"F0.imprint","IMPRINT",FACE,{"disambiguationData":[TD([[makeQuery(id+"F0.imprint","IMPRINT",EDGE,{"derivedFrom":subQ0}),-1.0]])]});}
            var Q54;
            {var subQ0=sQuery(id+"F0.wireOp",EDGE,"1b435d11-bbf8-4d76-92a6-f0dfc75fd8fa.rect.right");Q54=makeQuery(id+"F0.imprint","IMPRINT",FACE,{"disambiguationData":[TD([[makeQuery(id+"F0.imprint","IMPRINT",EDGE,{"derivedFrom":subQ0}),1.0]])]});}
            var Q55;
            {var subQ3=sQuery(id+"F0.wireOp",EDGE,"e5a37d3b-96b8-4f85-b028-1329ce64cde0.rect.top");Q55=makeQuery(id+"F0.imprint","IMPRINT",FACE,{"disambiguationData":[TD([[makeQuery(id+"F0.imprint","IMPRINT",EDGE,{"derivedFrom":subQ3}),-1.0]])]});}
            var Q56;
            {var subQ3=sQuery(id+"F0.wireOp",EDGE,"e5a37d3b-96b8-4f85-b028-1329ce64cde0.rect.bottom");Q56=makeQuery(id+"F0.imprint","IMPRINT",FACE,{"disambiguationData":[TD([[makeQuery(id+"F0.imprint","IMPRINT",EDGE,{"derivedFrom":subQ3}),1.0]])]});}
            var Q57;
            {var subQ1=sQuery(id+"F0.wireOp",EDGE,"17f1270a-2747-4b10-848f-e92c6a9a448e.rect.bottom");Q57=makeQuery(id+"F0.imprint","IMPRINT",FACE,{"disambiguationData":[TD([[makeQuery(id+"F0.imprint","IMPRINT",EDGE,{"derivedFrom":subQ1}),-1.0]])]});}
            var Q58;
            {var subQ1=sQuery(id+"F0.wireOp",EDGE,"b581c809-2514-4fc4-bae3-9c6477576331.rect.bottom");Q58=makeQuery(id+"F0.imprint","IMPRINT",FACE,{"disambiguationData":[TD([[makeQuery(id+"F0.imprint","IMPRINT",EDGE,{"derivedFrom":subQ1}),-1.0]])]});}
            var Q59;
            Q59=makeQuery(id+"F0.imprint","IMPRINT",FACE,{"disambiguationData":[TD([[makeQuery(id+"F0.imprint","IMPRINT",EDGE,{"derivedFrom":sQuery(id+"F0.wireOp",EDGE,"575d105f-47f6-455c-9778-bb3c833a7581.rect.bottom")}),-1.0]])]});
            var Q60;
            {var subQ1=sQuery(id+"F0.wireOp",EDGE,"fff48876-04e1-4fc8-9402-123f03e55176.rect.bottom");Q60=makeQuery(id+"F0.imprint","IMPRINT",FACE,{"disambiguationData":[TD([[makeQuery(id+"F0.imprint","IMPRINT",EDGE,{"derivedFrom":subQ1}),1.0]])]});}
            var Q61;
            {var subQ1=sQuery(id+"F0.wireOp",EDGE,"13d43389-c631-4c73-802b-5182c9e3e657.rect.bottom");Q61=makeQuery(id+"F0.imprint","IMPRINT",FACE,{"disambiguationData":[TD([[makeQuery(id+"F0.imprint","IMPRINT",EDGE,{"derivedFrom":subQ1}),1.0]])]});}
            var Q62;
            Q62=makeQuery(id+"F0.imprint","IMPRINT",FACE,{"disambiguationData":[TD([[makeQuery(id+"F0.imprint","IMPRINT",EDGE,{"derivedFrom":sQuery(id+"F0.wireOp",EDGE,"7228705b-8608-42c8-9eaf-56973434d279.rect.bottom")}),1.0]])]});
            var Q63;
            {var subQ1=sQuery(id+"F0.wireOp",EDGE,"a5fb6563-f1c4-4e54-b2d2-c845c3ec7855.rect.bottom");Q63=makeQuery(id+"F0.imprint","IMPRINT",FACE,{"disambiguationData":[TD([[makeQuery(id+"F0.imprint","IMPRINT",EDGE,{"derivedFrom":subQ1}),-1.0]])]});}
            var Q64;
            {var subQ1=sQuery(id+"F0.wireOp",EDGE,"528f5d14-1237-4880-831d-745eabb57258.rect.bottom");Q64=makeQuery(id+"F0.imprint","IMPRINT",FACE,{"disambiguationData":[TD([[makeQuery(id+"F0.imprint","IMPRINT",EDGE,{"derivedFrom":subQ1}),-1.0]])]});}
            var Q65;
            {var subQ1=sQuery(id+"F0.wireOp",EDGE,"3a1d95bb-315e-45e8-9574-3d48fc663a87.rect.bottom");Q65=makeQuery(id+"F0.imprint","IMPRINT",FACE,{"disambiguationData":[TD([[makeQuery(id+"F0.imprint","IMPRINT",EDGE,{"derivedFrom":subQ1}),-1.0]])]});}
            var Q66;
            Q66=makeQuery(id+"F0.imprint","IMPRINT",FACE,{"disambiguationData":[TD([[makeQuery(id+"F0.imprint","IMPRINT",EDGE,{"derivedFrom":sQuery(id+"F0.wireOp",EDGE,"9606da7c-27d0-4a8d-8844-21ce520e0263.rect.bottom")}),1.0]])]});
            var Q67;
            {var subQ1=sQuery(id+"F0.wireOp",EDGE,"2a591dfd-ceba-4041-ab34-b8e9dd08917c.rect.bottom");Q67=makeQuery(id+"F0.imprint","IMPRINT",FACE,{"disambiguationData":[TD([[makeQuery(id+"F0.imprint","IMPRINT",EDGE,{"derivedFrom":subQ1}),-1.0]])]});}
            var Q68;
            {var subQ1=sQuery(id+"F0.wireOp",EDGE,"a0e47c1a-8269-4cee-a721-aee1dfa80837.rect.bottom");Q68=makeQuery(id+"F0.imprint","IMPRINT",FACE,{"disambiguationData":[TD([[makeQuery(id+"F0.imprint","IMPRINT",EDGE,{"derivedFrom":subQ1}),-1.0]])]});}
            var Q69;
            Q69=makeQuery(id+"F0.imprint","IMPRINT",FACE,{"disambiguationData":[TD([[makeQuery(id+"F0.imprint","IMPRINT",EDGE,{"derivedFrom":sQuery(id+"F0.wireOp",EDGE,"E35.rect.bottom")}),-1.0]])]});
            var Q70;
            Q70=makeQuery(id+"F0.imprint","IMPRINT",FACE,{"disambiguationData":[TD([[makeQuery(id+"F0.imprint","IMPRINT",EDGE,{"derivedFrom":sQuery(id+"F0.wireOp",EDGE,"E32.rect.top")}),-1.0]])]});
            var Q71;
            Q71=makeQuery(id+"F0.imprint","IMPRINT",FACE,{"disambiguationData":[TD([[makeQuery(id+"F0.imprint","IMPRINT",EDGE,{"derivedFrom":sQuery(id+"F0.wireOp",EDGE,"E32.rect.bottom")}),-1.0]])]});
            var Q72;
            Q72=makeQuery(id+"F0.imprint","IMPRINT",FACE,{"disambiguationData":[TD([[makeQuery(id+"F0.imprint","IMPRINT",EDGE,{"derivedFrom":sQuery(id+"F0.wireOp",EDGE,"E45")}),1.0]])]});
            var Q73;
            Q73=makeQuery(id+"F0.imprint","IMPRINT",FACE,{"disambiguationData":[TD([[makeQuery(id+"F0.imprint","IMPRINT",EDGE,{"derivedFrom":sQuery(id+"F0.wireOp",EDGE,"E46")}),1.0]])]});
            var Q74;
            Q74=makeQuery(id+"F0.imprint","IMPRINT",FACE,{"disambiguationData":[TD([[makeQuery(id+"F0.imprint","IMPRINT",EDGE,{"derivedFrom":sQuery(id+"F0.wireOp",EDGE,"E48")}),1.0]])]});
            var Q75;
            Q75=makeQuery(id+"F0.imprint","IMPRINT",FACE,{"disambiguationData":[TD([[makeQuery(id+"F0.imprint","IMPRINT",EDGE,{"derivedFrom":sQuery(id+"F0.wireOp",EDGE,"E47")}),1.0]])]});
            var Q76;
            Q76=makeQuery(id+"F0.imprint","IMPRINT",FACE,{"disambiguationData":[TD([[makeQuery(id+"F0.imprint","IMPRINT",EDGE,{"derivedFrom":sQuery(id+"F0.wireOp",EDGE,"E50")}),1.0]])]});
            var Q77;
            Q77=makeQuery(id+"F0.imprint","IMPRINT",FACE,{"disambiguationData":[TD([[makeQuery(id+"F0.imprint","IMPRINT",EDGE,{"derivedFrom":sQuery(id+"F0.wireOp",EDGE,"E49")}),1.0]])]});
            var Q78;
            Q78=makeQuery(id+"F0.imprint","IMPRINT",FACE,{"disambiguationData":[TD([[makeQuery(id+"F0.imprint","IMPRINT",EDGE,{"derivedFrom":sQuery(id+"F0.wireOp",EDGE,"E33")}),1.0]])]});
            var Q79;
            Q79=makeQuery(id+"F0.imprint","IMPRINT",FACE,{"disambiguationData":[TD([[makeQuery(id+"F0.imprint","IMPRINT",EDGE,{"derivedFrom":sQuery(id+"F0.wireOp",EDGE,"E56.rect.bottom")}),1.0]])]});
            var Q80;
            {var subQ1=sQuery(id+"F0.wireOp",EDGE,"E57.rect.bottom");Q80=makeQuery(id+"F0.imprint","IMPRINT",FACE,{"disambiguationData":[TD([[makeQuery(id+"F0.imprint","IMPRINT",EDGE,{"derivedFrom":subQ1}),1.0]])]});}
            var Q81;
            {var subQ1=sQuery(id+"F0.wireOp",EDGE,"E59.rect.bottom");Q81=makeQuery(id+"F0.imprint","IMPRINT",FACE,{"disambiguationData":[TD([[makeQuery(id+"F0.imprint","IMPRINT",EDGE,{"derivedFrom":subQ1}),1.0]])]});}
            var Q82;
            {var subQ1=sQuery(id+"F0.wireOp",EDGE,"E55.rect.bottom");Q82=makeQuery(id+"F0.imprint","IMPRINT",FACE,{"disambiguationData":[TD([[makeQuery(id+"F0.imprint","IMPRINT",EDGE,{"derivedFrom":subQ1}),1.0]])]});}
            var Q83;
            Q83=makeQuery(id+"F0.imprint","IMPRINT",FACE,{"disambiguationData":[TD([[makeQuery(id+"F0.imprint","IMPRINT",EDGE,{"derivedFrom":sQuery(id+"F0.wireOp",EDGE,"E54.rect.bottom")}),-1.0]])]});
            var Q84;
            {var subQ0=sQuery(id+"F0.wireOp",EDGE,"E51.rect.bottom");Q84=makeQuery(id+"F0.imprint","IMPRINT",FACE,{"disambiguationData":[TD([[makeQuery(id+"F0.imprint","IMPRINT",EDGE,{"derivedFrom":subQ0}),-1.0]])]});}
            var Q85;
            {var subQ1=sQuery(id+"F0.wireOp",EDGE,"E52.rect.bottom");Q85=makeQuery(id+"F0.imprint","IMPRINT",FACE,{"disambiguationData":[TD([[makeQuery(id+"F0.imprint","IMPRINT",EDGE,{"derivedFrom":subQ1}),1.0]])]});}
            var Q86;
            {var subQ0=sQuery(id+"F0.wireOp",EDGE,"E62.rect.bottom");Q86=makeQuery(id+"F0.imprint","IMPRINT",FACE,{"disambiguationData":[TD([[makeQuery(id+"F0.imprint","IMPRINT",EDGE,{"derivedFrom":subQ0}),-1.0]])]});}
            var Q87;
            Q87=makeQuery(id+"F0.imprint","IMPRINT",FACE,{"disambiguationData":[TD([[makeQuery(id+"F0.imprint","IMPRINT",EDGE,{"derivedFrom":sQuery(id+"F0.wireOp",EDGE,"E53.rect.bottom")}),1.0]])]});
            var Q88;
            Q88=makeQuery(id+"F0.imprint","IMPRINT",FACE,{"disambiguationData":[TD([[makeQuery(id+"F0.imprint","IMPRINT",EDGE,{"derivedFrom":sQuery(id+"F0.wireOp",EDGE,"E64.rect.bottom")}),1.0]])]});
            var Q89;
            {var subQ1=sQuery(id+"F0.wireOp",EDGE,"E63.rect.bottom");Q89=makeQuery(id+"F0.imprint","IMPRINT",FACE,{"disambiguationData":[TD([[makeQuery(id+"F0.imprint","IMPRINT",EDGE,{"derivedFrom":subQ1}),1.0]])]});}
            var Q90;
            {var subQ1=sQuery(id+"F0.wireOp",EDGE,"E69.rect.bottom");Q90=makeQuery(id+"F0.imprint","IMPRINT",FACE,{"disambiguationData":[TD([[makeQuery(id+"F0.imprint","IMPRINT",EDGE,{"derivedFrom":subQ1}),1.0]])]});}
            var Q91;
            Q91=makeQuery(id+"F0.imprint","IMPRINT",FACE,{"disambiguationData":[TD([[makeQuery(id+"F0.imprint","IMPRINT",EDGE,{"derivedFrom":sQuery(id+"F0.wireOp",EDGE,"E58.rect.bottom")}),1.0]])]});
            var Q92;
            Q92=makeQuery(id+"F0.imprint","IMPRINT",FACE,{"disambiguationData":[TD([[makeQuery(id+"F0.imprint","IMPRINT",EDGE,{"derivedFrom":sQuery(id+"F0.wireOp",EDGE,"E61.rect.bottom")}),-1.0]])]});
            var Q93;
            {var subQ1=sQuery(id+"F0.wireOp",EDGE,"E60.rect.bottom");Q93=makeQuery(id+"F0.imprint","IMPRINT",FACE,{"disambiguationData":[TD([[makeQuery(id+"F0.imprint","IMPRINT",EDGE,{"derivedFrom":subQ1}),1.0]])]});}
            var Q94;
            {var subQ1=sQuery(id+"F0.wireOp",EDGE,"E70.rect.bottom");Q94=makeQuery(id+"F0.imprint","IMPRINT",FACE,{"disambiguationData":[TD([[makeQuery(id+"F0.imprint","IMPRINT",EDGE,{"derivedFrom":subQ1}),1.0]])]});}
            var Q95;
            {var subQ1=sQuery(id+"F0.wireOp",EDGE,"E73.rect.bottom");Q95=makeQuery(id+"F0.imprint","IMPRINT",FACE,{"disambiguationData":[TD([[makeQuery(id+"F0.imprint","IMPRINT",EDGE,{"derivedFrom":subQ1}),-1.0]])]});}
            var Q96;
            Q96=makeQuery(id+"F0.imprint","IMPRINT",FACE,{"disambiguationData":[TD([[makeQuery(id+"F0.imprint","IMPRINT",EDGE,{"derivedFrom":sQuery(id+"F0.wireOp",EDGE,"E65.rect.bottom")}),-1.0]])]});
            var Q97;
            {var subQ1=sQuery(id+"F0.wireOp",EDGE,"E66.rect.bottom");Q97=makeQuery(id+"F0.imprint","IMPRINT",FACE,{"disambiguationData":[TD([[makeQuery(id+"F0.imprint","IMPRINT",EDGE,{"derivedFrom":subQ1}),1.0]])]});}
            var Q98;
            {var subQ0=sQuery(id+"F0.wireOp",EDGE,"E67.rect.bottom");Q98=makeQuery(id+"F0.imprint","IMPRINT",FACE,{"disambiguationData":[TD([[makeQuery(id+"F0.imprint","IMPRINT",EDGE,{"derivedFrom":subQ0}),1.0]])]});}
            var Q99;
            {var subQ1=sQuery(id+"F0.wireOp",EDGE,"E72.rect.bottom");Q99=makeQuery(id+"F0.imprint","IMPRINT",FACE,{"disambiguationData":[TD([[makeQuery(id+"F0.imprint","IMPRINT",EDGE,{"derivedFrom":subQ1}),-1.0]])]});}
            var Q100;
            Q100=makeQuery(id+"F0.imprint","IMPRINT",FACE,{"disambiguationData":[TD([[makeQuery(id+"F0.imprint","IMPRINT",EDGE,{"derivedFrom":sQuery(id+"F0.wireOp",EDGE,"E68.rect.bottom")}),1.0]])]});
            var Q101;
            Q101=makeQuery(id+"F0.imprint","IMPRINT",FACE,{"disambiguationData":[TD([[makeQuery(id+"F0.imprint","IMPRINT",EDGE,{"derivedFrom":sQuery(id+"F0.wireOp",EDGE,"E71.rect.bottom")}),1.0]])]});
            extrude(context, id + "F1", {"entities" : qUnion([Q0, Q1, Q2, Q3, Q4, Q5, Q6, Q7, Q8, Q9, Q10, Q11, Q12, Q13, Q14, Q15, Q16, Q17, Q18, Q19, Q20, Q21, Q22, Q23, Q24, Q25, Q26, Q27, Q28, Q29, Q30, Q31, Q32, Q33, Q34, Q35, Q36, Q37, Q38, Q39, Q40, Q41, Q42, Q43, Q44, Q45, Q46, Q47, Q48, Q49, Q50, Q51, Q52, Q53, Q54, Q55, Q56, Q57, Q58, Q59, Q60, Q61, Q62, Q63, Q64, Q65, Q66, Q67, Q68, Q69, Q70, Q71, Q72, Q73, Q74, Q75, Q76, Q77, Q78, Q79, Q80, Q81, Q82, Q83, Q84, Q85, Q86, Q87, Q88, Q89, Q90, Q91, Q92, Q93, Q94, Q95, Q96, Q97, Q98, Q99, Q100, Q101]), "oppositeDirection" : true, "depth" : 4 * mm});
        }
        {
            var Q0;
            {var subQ1=sQuery(id+"F0.wireOp",EDGE,"839c260c-2e27-47bf-a2f2-8bfdeadb8496.2");var subQ3=sQuery(id+"F0.wireOp",EDGE,"839c260c-2e27-47bf-a2f2-8bfdeadb8496.1");var subQ5=makeQuery(id+"F0.imprint","INTERSECT",VERTEX,{"derivedFrom":[subQ3,subQ1]});Q0=makeQuery(id+"F0.imprint","IMPRINT",FACE,{"disambiguationData":[TD([[makeQuery(id+"F0.imprint","IMPRINT",EDGE,{"disambiguationData":[TD([[subQ5,1.0]])],"derivedFrom":subQ3}),-1.0]])]});}
            var Q1;
            {var subQ1=sQuery(id+"F0.wireOp",EDGE,"839c260c-2e27-47bf-a2f2-8bfdeadb8496.2");var subQ3=sQuery(id+"F0.wireOp",EDGE,"839c260c-2e27-47bf-a2f2-8bfdeadb8496.1");var subQ5=makeQuery(id+"F0.imprint","INTERSECT",VERTEX,{"derivedFrom":[subQ3,subQ1]});Q1=makeQuery(id+"F0.imprint","IMPRINT",FACE,{"disambiguationData":[TD([[makeQuery(id+"F0.imprint","IMPRINT",EDGE,{"disambiguationData":[TD([[subQ5,1.0]])],"derivedFrom":subQ3}),1.0]])]});}
            var Q2;
            {var subQ1=sQuery(id+"F0.wireOp",EDGE,"839c260c-2e27-47bf-a2f2-8bfdeadb8496.3");var subQ3=sQuery(id+"F0.wireOp",EDGE,"839c260c-2e27-47bf-a2f2-8bfdeadb8496.2");var subQ5=makeQuery(id+"F0.imprint","INTERSECT",VERTEX,{"derivedFrom":[subQ3,subQ1]});Q2=makeQuery(id+"F0.imprint","IMPRINT",FACE,{"disambiguationData":[TD([[makeQuery(id+"F0.imprint","IMPRINT",EDGE,{"disambiguationData":[TD([[subQ5,1.0]])],"derivedFrom":subQ3}),1.0]])]});}
            var Q3;
            {var subQ1=sQuery(id+"F0.wireOp",EDGE,"839c260c-2e27-47bf-a2f2-8bfdeadb8496.3");var subQ3=sQuery(id+"F0.wireOp",EDGE,"839c260c-2e27-47bf-a2f2-8bfdeadb8496.2");var subQ5=makeQuery(id+"F0.imprint","INTERSECT",VERTEX,{"derivedFrom":[subQ3,subQ1]});Q3=makeQuery(id+"F0.imprint","IMPRINT",FACE,{"disambiguationData":[TD([[makeQuery(id+"F0.imprint","IMPRINT",EDGE,{"disambiguationData":[TD([[subQ5,1.0]])],"derivedFrom":subQ3}),-1.0]])]});}
            var Q4;
            {var subQ1=sQuery(id+"F0.wireOp",EDGE,"839c260c-2e27-47bf-a2f2-8bfdeadb8496.3");var subQ3=sQuery(id+"F0.wireOp",EDGE,"839c260c-2e27-47bf-a2f2-8bfdeadb8496.0");var subQ5=makeQuery(id+"F0.imprint","INTERSECT",VERTEX,{"derivedFrom":[subQ3,subQ1]});Q4=makeQuery(id+"F0.imprint","IMPRINT",FACE,{"disambiguationData":[TD([[makeQuery(id+"F0.imprint","IMPRINT",EDGE,{"disambiguationData":[TD([[subQ5,1.0]])],"derivedFrom":subQ3}),-1.0]])]});}
            var Q5;
            {var subQ1=sQuery(id+"F0.wireOp",EDGE,"839c260c-2e27-47bf-a2f2-8bfdeadb8496.3");var subQ3=sQuery(id+"F0.wireOp",EDGE,"839c260c-2e27-47bf-a2f2-8bfdeadb8496.0");var subQ5=makeQuery(id+"F0.imprint","INTERSECT",VERTEX,{"derivedFrom":[subQ3,subQ1]});Q5=makeQuery(id+"F0.imprint","IMPRINT",FACE,{"disambiguationData":[TD([[makeQuery(id+"F0.imprint","IMPRINT",EDGE,{"disambiguationData":[TD([[subQ5,1.0]])],"derivedFrom":subQ3}),1.0]])]});}
            var Q6;
            {var subQ0=sQuery(id+"F0.wireOp",EDGE,"E24");var subQ3=sQuery(id+"F0.wireOp",EDGE,"839c260c-2e27-47bf-a2f2-8bfdeadb8496.0");var subQ4=makeQuery(id+"F0.imprint","INTERSECT",VERTEX,{"derivedFrom":[subQ3,subQ0]});Q6=makeQuery(id+"F0.imprint","IMPRINT",FACE,{"disambiguationData":[TD([[makeQuery(id+"F0.imprint","IMPRINT",EDGE,{"disambiguationData":[TD([[subQ4,-1.0]])],"derivedFrom":subQ3}),-1.0]])]});}
            var Q7;
            {var subQ0=sQuery(id+"F0.wireOp",EDGE,"E24");var subQ3=sQuery(id+"F0.wireOp",EDGE,"839c260c-2e27-47bf-a2f2-8bfdeadb8496.0");var subQ4=makeQuery(id+"F0.imprint","INTERSECT",VERTEX,{"derivedFrom":[subQ3,subQ0]});Q7=makeQuery(id+"F0.imprint","IMPRINT",FACE,{"disambiguationData":[TD([[makeQuery(id+"F0.imprint","IMPRINT",EDGE,{"disambiguationData":[TD([[subQ4,-1.0]])],"derivedFrom":subQ3}),1.0]])]});}
            var Q8;
            Q8=makeQuery(id+"F0.imprint","IMPRINT",FACE,{"disambiguationData":[TD([[makeQuery(id+"F0.imprint","IMPRINT",EDGE,{"derivedFrom":sQuery(id+"F0.wireOp",EDGE,"E0.bottom")}),-1.0]])]});
            extrude(context, id + "F2", {"entities" : qUnion([Q0, Q1, Q2, Q3, Q4, Q5, Q6, Q7, Q8]), "operationType" : NewBodyOperationType.ADD, "depth" : 4 * mm});
        }
        {
            var Q0;
            Q0=makeQuery(id+"F0.imprint","IMPRINT",FACE,{"disambiguationData":[TD([[makeQuery(id+"F0.imprint","IMPRINT",EDGE,{"derivedFrom":sQuery(id+"F0.wireOp",EDGE,"E13.bottom")}),-1.0]])]});
            var Q1;
            Q1=makeQuery(id+"F0.imprint","IMPRINT",FACE,{"disambiguationData":[TD([[makeQuery(id+"F0.imprint","IMPRINT",EDGE,{"derivedFrom":sQuery(id+"F0.wireOp",EDGE,"E7.left")}),1.0]])]});
            var Q2;
            Q2=makeQuery(id+"F0.imprint","IMPRINT",FACE,{"disambiguationData":[TD([[makeQuery(id+"F0.imprint","IMPRINT",EDGE,{"derivedFrom":sQuery(id+"F0.wireOp",EDGE,"E14.right")}),1.0]])]});
            var Q3;
            Q3=makeQuery(id+"F0.imprint","IMPRINT",FACE,{"disambiguationData":[TD([[makeQuery(id+"F0.imprint","IMPRINT",EDGE,{"derivedFrom":sQuery(id+"F0.wireOp",EDGE,"E15.rect.bottom")}),1.0]])]});
            var Q4;
            Q4=makeQuery(id+"F0.imprint","IMPRINT",FACE,{"disambiguationData":[TD([[makeQuery(id+"F0.imprint","IMPRINT",EDGE,{"derivedFrom":sQuery(id+"F0.wireOp",EDGE,"E8.bottom")}),-1.0]])]});
            var Q5;
            Q5=makeQuery(id+"F0.imprint","IMPRINT",FACE,{"disambiguationData":[TD([[makeQuery(id+"F0.imprint","IMPRINT",EDGE,{"derivedFrom":sQuery(id+"F0.wireOp",EDGE,"E6.top")}),-1.0]])]});
            var Q6;
            Q6=makeQuery(id+"F0.imprint","IMPRINT",FACE,{"disambiguationData":[TD([[makeQuery(id+"F0.imprint","IMPRINT",EDGE,{"derivedFrom":sQuery(id+"F0.wireOp",EDGE,"E11.bottom")}),1.0]])]});
            var Q7;
            Q7=makeQuery(id+"F0.imprint","IMPRINT",FACE,{"disambiguationData":[TD([[makeQuery(id+"F0.imprint","IMPRINT",EDGE,{"derivedFrom":sQuery(id+"F0.wireOp",EDGE,"E17.1.0.34")}),1.0]])]});
            var Q8;
            Q8=makeQuery(id+"F0.imprint","IMPRINT",FACE,{"disambiguationData":[TD([[makeQuery(id+"F0.imprint","IMPRINT",EDGE,{"derivedFrom":sQuery(id+"F0.wireOp",EDGE,"E17.1.0.35")}),-1.0]])]});
            var Q9;
            Q9=makeQuery(id+"F0.imprint","IMPRINT",FACE,{"disambiguationData":[TD([[makeQuery(id+"F0.imprint","IMPRINT",EDGE,{"derivedFrom":sQuery(id+"F0.wireOp",EDGE,"E17.1.0.12")}),-1.0]])]});
            var Q10;
            Q10=makeQuery(id+"F0.imprint","IMPRINT",FACE,{"disambiguationData":[TD([[makeQuery(id+"F0.imprint","IMPRINT",EDGE,{"derivedFrom":sQuery(id+"F0.wireOp",EDGE,"E17.1.0.38")}),1.0]])]});
            var Q11;
            Q11=makeQuery(id+"F0.imprint","IMPRINT",FACE,{"disambiguationData":[TD([[makeQuery(id+"F0.imprint","IMPRINT",EDGE,{"derivedFrom":sQuery(id+"F0.wireOp",EDGE,"E17.1.0.15")}),-1.0]])]});
            var Q12;
            Q12=makeQuery(id+"F0.imprint","IMPRINT",FACE,{"disambiguationData":[TD([[makeQuery(id+"F0.imprint","IMPRINT",EDGE,{"derivedFrom":sQuery(id+"F0.wireOp",EDGE,"E17.1.0.5")}),1.0]])]});
            var Q13;
            Q13=makeQuery(id+"F0.imprint","IMPRINT",FACE,{"disambiguationData":[TD([[makeQuery(id+"F0.imprint","IMPRINT",EDGE,{"derivedFrom":sQuery(id+"F0.wireOp",EDGE,"E17.1.0.7")}),-1.0]])]});
            var Q14;
            Q14=makeQuery(id+"F0.imprint","IMPRINT",FACE,{"disambiguationData":[TD([[makeQuery(id+"F0.imprint","IMPRINT",EDGE,{"derivedFrom":sQuery(id+"F0.wireOp",EDGE,"E17.2.0.15")}),-1.0]])]});
            var Q15;
            Q15=makeQuery(id+"F0.imprint","IMPRINT",FACE,{"disambiguationData":[TD([[makeQuery(id+"F0.imprint","IMPRINT",EDGE,{"derivedFrom":sQuery(id+"F0.wireOp",EDGE,"E17.2.0.5")}),1.0]])]});
            var Q16;
            Q16=makeQuery(id+"F0.imprint","IMPRINT",FACE,{"disambiguationData":[TD([[makeQuery(id+"F0.imprint","IMPRINT",EDGE,{"derivedFrom":sQuery(id+"F0.wireOp",EDGE,"E17.2.0.7")}),-1.0]])]});
            var Q17;
            Q17=makeQuery(id+"F0.imprint","IMPRINT",FACE,{"disambiguationData":[TD([[makeQuery(id+"F0.imprint","IMPRINT",EDGE,{"derivedFrom":sQuery(id+"F0.wireOp",EDGE,"E17.2.0.38")}),1.0]])]});
            var Q18;
            Q18=makeQuery(id+"F0.imprint","IMPRINT",FACE,{"disambiguationData":[TD([[makeQuery(id+"F0.imprint","IMPRINT",EDGE,{"derivedFrom":sQuery(id+"F0.wireOp",EDGE,"E17.2.0.12")}),-1.0]])]});
            var Q19;
            Q19=makeQuery(id+"F0.imprint","IMPRINT",FACE,{"disambiguationData":[TD([[makeQuery(id+"F0.imprint","IMPRINT",EDGE,{"derivedFrom":sQuery(id+"F0.wireOp",EDGE,"E17.2.0.34")}),1.0]])]});
            var Q20;
            Q20=makeQuery(id+"F0.imprint","IMPRINT",FACE,{"disambiguationData":[TD([[makeQuery(id+"F0.imprint","IMPRINT",EDGE,{"derivedFrom":sQuery(id+"F0.wireOp",EDGE,"E17.2.0.35")}),-1.0]])]});
            var Q21;
            Q21=makeQuery(id+"F0.imprint","IMPRINT",FACE,{"disambiguationData":[TD([[makeQuery(id+"F0.imprint","IMPRINT",EDGE,{"derivedFrom":sQuery(id+"F0.wireOp",EDGE,"E17.3.0.35")}),-1.0]])]});
            var Q22;
            Q22=makeQuery(id+"F0.imprint","IMPRINT",FACE,{"disambiguationData":[TD([[makeQuery(id+"F0.imprint","IMPRINT",EDGE,{"derivedFrom":sQuery(id+"F0.wireOp",EDGE,"E17.3.0.34")}),1.0]])]});
            var Q23;
            Q23=makeQuery(id+"F0.imprint","IMPRINT",FACE,{"disambiguationData":[TD([[makeQuery(id+"F0.imprint","IMPRINT",EDGE,{"derivedFrom":sQuery(id+"F0.wireOp",EDGE,"E17.3.0.12")}),-1.0]])]});
            var Q24;
            Q24=makeQuery(id+"F0.imprint","IMPRINT",FACE,{"disambiguationData":[TD([[makeQuery(id+"F0.imprint","IMPRINT",EDGE,{"derivedFrom":sQuery(id+"F0.wireOp",EDGE,"E17.3.0.38")}),1.0]])]});
            var Q25;
            Q25=makeQuery(id+"F0.imprint","IMPRINT",FACE,{"disambiguationData":[TD([[makeQuery(id+"F0.imprint","IMPRINT",EDGE,{"derivedFrom":sQuery(id+"F0.wireOp",EDGE,"E17.3.0.15")}),-1.0]])]});
            var Q26;
            Q26=makeQuery(id+"F0.imprint","IMPRINT",FACE,{"disambiguationData":[TD([[makeQuery(id+"F0.imprint","IMPRINT",EDGE,{"derivedFrom":sQuery(id+"F0.wireOp",EDGE,"E17.3.0.7")}),-1.0]])]});
            var Q27;
            Q27=makeQuery(id+"F0.imprint","IMPRINT",FACE,{"disambiguationData":[TD([[makeQuery(id+"F0.imprint","IMPRINT",EDGE,{"derivedFrom":sQuery(id+"F0.wireOp",EDGE,"E17.3.0.5")}),1.0]])]});
            var Q28;
            Q28=makeQuery(id+"F0.imprint","IMPRINT",FACE,{"disambiguationData":[TD([[makeQuery(id+"F0.imprint","IMPRINT",EDGE,{"derivedFrom":sQuery(id+"F0.wireOp",EDGE,"E23")}),1.0]])]});
            var Q29;
            Q29=makeQuery(id+"F0.imprint","IMPRINT",FACE,{"disambiguationData":[TD([[makeQuery(id+"F0.imprint","IMPRINT",EDGE,{"derivedFrom":sQuery(id+"F0.wireOp",EDGE,"E22")}),1.0]])]});
            var Q30;
            Q30=makeQuery(id+"F0.imprint","IMPRINT",FACE,{"disambiguationData":[TD([[makeQuery(id+"F0.imprint","IMPRINT",EDGE,{"derivedFrom":sQuery(id+"F0.wireOp",EDGE,"E18.1.0.36")}),1.0]])]});
            var Q31;
            Q31=makeQuery(id+"F0.imprint","IMPRINT",FACE,{"disambiguationData":[TD([[makeQuery(id+"F0.imprint","IMPRINT",EDGE,{"derivedFrom":sQuery(id+"F0.wireOp",EDGE,"E18.1.0.61")}),1.0]])]});
            var Q32;
            Q32=makeQuery(id+"F0.imprint","IMPRINT",FACE,{"disambiguationData":[TD([[makeQuery(id+"F0.imprint","IMPRINT",EDGE,{"derivedFrom":sQuery(id+"F0.wireOp",EDGE,"E18.1.0.38")}),1.0]])]});
            var Q33;
            Q33=makeQuery(id+"F0.imprint","IMPRINT",FACE,{"disambiguationData":[TD([[makeQuery(id+"F0.imprint","IMPRINT",EDGE,{"derivedFrom":sQuery(id+"F0.wireOp",EDGE,"E18.1.0.53")}),-1.0]])]});
            var Q34;
            Q34=makeQuery(id+"F0.imprint","IMPRINT",FACE,{"disambiguationData":[TD([[makeQuery(id+"F0.imprint","IMPRINT",EDGE,{"derivedFrom":sQuery(id+"F0.wireOp",EDGE,"E18.1.0.54")}),1.0]])]});
            var Q35;
            Q35=makeQuery(id+"F0.imprint","IMPRINT",FACE,{"disambiguationData":[TD([[makeQuery(id+"F0.imprint","IMPRINT",EDGE,{"derivedFrom":sQuery(id+"F0.wireOp",EDGE,"E19.1.0.53")}),-1.0]])]});
            var Q36;
            Q36=makeQuery(id+"F0.imprint","IMPRINT",FACE,{"disambiguationData":[TD([[makeQuery(id+"F0.imprint","IMPRINT",EDGE,{"derivedFrom":sQuery(id+"F0.wireOp",EDGE,"E19.1.0.51")}),1.0]])]});
            var Q37;
            Q37=makeQuery(id+"F0.imprint","IMPRINT",FACE,{"disambiguationData":[TD([[makeQuery(id+"F0.imprint","IMPRINT",EDGE,{"derivedFrom":sQuery(id+"F0.wireOp",EDGE,"E18.1.0.51")}),1.0]])]});
            var Q38;
            Q38=makeQuery(id+"F0.imprint","IMPRINT",FACE,{"disambiguationData":[TD([[makeQuery(id+"F0.imprint","IMPRINT",EDGE,{"derivedFrom":sQuery(id+"F0.wireOp",EDGE,"E18.1.0.5")}),1.0]])]});
            var Q39;
            {var subQ1=sQuery(id+"F0.wireOp",EDGE,"a5fb6563-f1c4-4e54-b2d2-c845c3ec7855.rect.bottom");Q39=makeQuery(id+"F0.imprint","IMPRINT",FACE,{"disambiguationData":[TD([[makeQuery(id+"F0.imprint","IMPRINT",EDGE,{"derivedFrom":subQ1}),-1.0]])]});}
            var Q40;
            Q40=makeQuery(id+"F0.imprint","IMPRINT",FACE,{"disambiguationData":[TD([[makeQuery(id+"F0.imprint","IMPRINT",EDGE,{"derivedFrom":sQuery(id+"F0.wireOp",EDGE,"E33")}),1.0]])]});
            extrude(context, id + "F3", {"entities" : qUnion([Q0, Q1, Q2, Q3, Q4, Q5, Q6, Q7, Q8, Q9, Q10, Q11, Q12, Q13, Q14, Q15, Q16, Q17, Q18, Q19, Q20, Q21, Q22, Q23, Q24, Q25, Q26, Q27, Q28, Q29, Q30, Q31, Q32, Q33, Q34, Q35, Q36, Q37, Q38, Q39, Q40]), "operationType" : NewBodyOperationType.REMOVE, "oppositeDirection" : true, "depth" : 3.7 * mm});
        }
        {
            var Q0;
            Q0=makeQuery(id+"F0.imprint","IMPRINT",FACE,{"disambiguationData":[TD([[makeQuery(id+"F0.imprint","IMPRINT",EDGE,{"derivedFrom":sQuery(id+"F0.wireOp",EDGE,"E58.rect.bottom")}),1.0]])]});
            var Q1;
            {var subQ1=sQuery(id+"F0.wireOp",EDGE,"E60.rect.bottom");Q1=makeQuery(id+"F0.imprint","IMPRINT",FACE,{"disambiguationData":[TD([[makeQuery(id+"F0.imprint","IMPRINT",EDGE,{"derivedFrom":subQ1}),1.0]])]});}
            var Q2;
            {var subQ1=sQuery(id+"F0.wireOp",EDGE,"E59.rect.bottom");Q2=makeQuery(id+"F0.imprint","IMPRINT",FACE,{"disambiguationData":[TD([[makeQuery(id+"F0.imprint","IMPRINT",EDGE,{"derivedFrom":subQ1}),1.0]])]});}
            var Q3;
            {var subQ1=sQuery(id+"F0.wireOp",EDGE,"E66.rect.bottom");Q3=makeQuery(id+"F0.imprint","IMPRINT",FACE,{"disambiguationData":[TD([[makeQuery(id+"F0.imprint","IMPRINT",EDGE,{"derivedFrom":subQ1}),1.0]])]});}
            var Q4;
            Q4=makeQuery(id+"F0.imprint","IMPRINT",FACE,{"disambiguationData":[TD([[makeQuery(id+"F0.imprint","IMPRINT",EDGE,{"derivedFrom":sQuery(id+"F0.wireOp",EDGE,"E65.rect.bottom")}),-1.0]])]});
            var Q5;
            {var subQ0=sQuery(id+"F0.wireOp",EDGE,"E67.rect.bottom");Q5=makeQuery(id+"F0.imprint","IMPRINT",FACE,{"disambiguationData":[TD([[makeQuery(id+"F0.imprint","IMPRINT",EDGE,{"derivedFrom":subQ0}),1.0]])]});}
            var Q6;
            {var subQ1=sQuery(id+"F0.wireOp",EDGE,"E72.rect.bottom");Q6=makeQuery(id+"F0.imprint","IMPRINT",FACE,{"disambiguationData":[TD([[makeQuery(id+"F0.imprint","IMPRINT",EDGE,{"derivedFrom":subQ1}),-1.0]])]});}
            var Q7;
            {var subQ1=sQuery(id+"F0.wireOp",EDGE,"E73.rect.bottom");Q7=makeQuery(id+"F0.imprint","IMPRINT",FACE,{"disambiguationData":[TD([[makeQuery(id+"F0.imprint","IMPRINT",EDGE,{"derivedFrom":subQ1}),-1.0]])]});}
            var Q8;
            {var subQ1=sQuery(id+"F0.wireOp",EDGE,"E70.rect.bottom");Q8=makeQuery(id+"F0.imprint","IMPRINT",FACE,{"disambiguationData":[TD([[makeQuery(id+"F0.imprint","IMPRINT",EDGE,{"derivedFrom":subQ1}),1.0]])]});}
            var Q9;
            Q9=makeQuery(id+"F0.imprint","IMPRINT",FACE,{"disambiguationData":[TD([[makeQuery(id+"F0.imprint","IMPRINT",EDGE,{"derivedFrom":sQuery(id+"F0.wireOp",EDGE,"E68.rect.bottom")}),1.0]])]});
            var Q10;
            {var subQ1=sQuery(id+"F0.wireOp",EDGE,"E69.rect.bottom");Q10=makeQuery(id+"F0.imprint","IMPRINT",FACE,{"disambiguationData":[TD([[makeQuery(id+"F0.imprint","IMPRINT",EDGE,{"derivedFrom":subQ1}),1.0]])]});}
            var Q11;
            Q11=makeQuery(id+"F0.imprint","IMPRINT",FACE,{"disambiguationData":[TD([[makeQuery(id+"F0.imprint","IMPRINT",EDGE,{"derivedFrom":sQuery(id+"F0.wireOp",EDGE,"E71.rect.bottom")}),1.0]])]});
            var Q12;
            {var subQ1=sQuery(id+"F0.wireOp",EDGE,"E63.rect.bottom");Q12=makeQuery(id+"F0.imprint","IMPRINT",FACE,{"disambiguationData":[TD([[makeQuery(id+"F0.imprint","IMPRINT",EDGE,{"derivedFrom":subQ1}),1.0]])]});}
            var Q13;
            Q13=makeQuery(id+"F0.imprint","IMPRINT",FACE,{"disambiguationData":[TD([[makeQuery(id+"F0.imprint","IMPRINT",EDGE,{"derivedFrom":sQuery(id+"F0.wireOp",EDGE,"E64.rect.bottom")}),1.0]])]});
            var Q14;
            {var subQ0=sQuery(id+"F0.wireOp",EDGE,"E62.rect.bottom");Q14=makeQuery(id+"F0.imprint","IMPRINT",FACE,{"disambiguationData":[TD([[makeQuery(id+"F0.imprint","IMPRINT",EDGE,{"derivedFrom":subQ0}),-1.0]])]});}
            var Q15;
            Q15=makeQuery(id+"F0.imprint","IMPRINT",FACE,{"disambiguationData":[TD([[makeQuery(id+"F0.imprint","IMPRINT",EDGE,{"derivedFrom":sQuery(id+"F0.wireOp",EDGE,"E61.rect.bottom")}),-1.0]])]});
            var Q16;
            {var subQ1=sQuery(id+"F0.wireOp",EDGE,"E55.rect.bottom");Q16=makeQuery(id+"F0.imprint","IMPRINT",FACE,{"disambiguationData":[TD([[makeQuery(id+"F0.imprint","IMPRINT",EDGE,{"derivedFrom":subQ1}),1.0]])]});}
            var Q17;
            Q17=makeQuery(id+"F0.imprint","IMPRINT",FACE,{"disambiguationData":[TD([[makeQuery(id+"F0.imprint","IMPRINT",EDGE,{"derivedFrom":sQuery(id+"F0.wireOp",EDGE,"E56.rect.bottom")}),1.0]])]});
            var Q18;
            {var subQ1=sQuery(id+"F0.wireOp",EDGE,"E57.rect.bottom");Q18=makeQuery(id+"F0.imprint","IMPRINT",FACE,{"disambiguationData":[TD([[makeQuery(id+"F0.imprint","IMPRINT",EDGE,{"derivedFrom":subQ1}),1.0]])]});}
            var Q19;
            {var subQ1=sQuery(id+"F0.wireOp",EDGE,"E52.rect.bottom");Q19=makeQuery(id+"F0.imprint","IMPRINT",FACE,{"disambiguationData":[TD([[makeQuery(id+"F0.imprint","IMPRINT",EDGE,{"derivedFrom":subQ1}),1.0]])]});}
            var Q20;
            Q20=makeQuery(id+"F0.imprint","IMPRINT",FACE,{"disambiguationData":[TD([[makeQuery(id+"F0.imprint","IMPRINT",EDGE,{"derivedFrom":sQuery(id+"F0.wireOp",EDGE,"E54.rect.bottom")}),-1.0]])]});
            var Q21;
            {var subQ0=sQuery(id+"F0.wireOp",EDGE,"E51.rect.bottom");Q21=makeQuery(id+"F0.imprint","IMPRINT",FACE,{"disambiguationData":[TD([[makeQuery(id+"F0.imprint","IMPRINT",EDGE,{"derivedFrom":subQ0}),-1.0]])]});}
            var Q22;
            Q22=makeQuery(id+"F0.imprint","IMPRINT",FACE,{"disambiguationData":[TD([[makeQuery(id+"F0.imprint","IMPRINT",EDGE,{"derivedFrom":sQuery(id+"F0.wireOp",EDGE,"E53.rect.bottom")}),1.0]])]});
            extrude(context, id + "F4", {"entities" : qUnion([Q0, Q1, Q2, Q3, Q4, Q5, Q6, Q7, Q8, Q9, Q10, Q11, Q12, Q13, Q14, Q15, Q16, Q17, Q18, Q19, Q20, Q21, Q22]), "operationType" : NewBodyOperationType.REMOVE, "oppositeDirection" : true, "depth" : 2 * mm});
        }
        {
            var Q0;
            {var subQ0=sQuery(id+"F0.wireOp",EDGE,"E0.top");var subQ1=sQuery(id+"F0.wireOp",EDGE,"E0.right");Q0=makeQuery(id+"F2.boolean.opBoolean","MERGE",EDGE,{"derivedFrom":[makeQuery(id+"F1.opExtrude","SWEPT_EDGE",EDGE,{"disambiguationData":[OSD([subQ0,subQ1])]}),makeQuery(id+"F2.opExtrude","SWEPT_EDGE",EDGE,{"disambiguationData":[OSD([subQ0,subQ1])]})]});}
            var Q1;
            {var subQ0=sQuery(id+"F0.wireOp",EDGE,"E0.bottom");var subQ1=sQuery(id+"F0.wireOp",EDGE,"E0.right");Q1=makeQuery(id+"F2.boolean.opBoolean","MERGE",EDGE,{"derivedFrom":[makeQuery(id+"F1.opExtrude","SWEPT_EDGE",EDGE,{"disambiguationData":[OSD([subQ0,subQ1])]}),makeQuery(id+"F2.opExtrude","SWEPT_EDGE",EDGE,{"disambiguationData":[OSD([subQ0,subQ1])]})]});}
            var Q2;
            {var subQ0=sQuery(id+"F0.wireOp",EDGE,"E0.top");var subQ1=sQuery(id+"F0.wireOp",EDGE,"E0.left");Q2=makeQuery(id+"F2.boolean.opBoolean","MERGE",EDGE,{"derivedFrom":[makeQuery(id+"F1.opExtrude","SWEPT_EDGE",EDGE,{"disambiguationData":[OSD([subQ0,subQ1])]}),makeQuery(id+"F2.opExtrude","SWEPT_EDGE",EDGE,{"disambiguationData":[OSD([subQ0,subQ1])]})]});}
            var Q3;
            {var subQ0=sQuery(id+"F0.wireOp",EDGE,"E0.bottom");var subQ1=sQuery(id+"F0.wireOp",EDGE,"E0.left");Q3=makeQuery(id+"F2.boolean.opBoolean","MERGE",EDGE,{"derivedFrom":[makeQuery(id+"F1.opExtrude","SWEPT_EDGE",EDGE,{"disambiguationData":[OSD([subQ0,subQ1])]}),makeQuery(id+"F2.opExtrude","SWEPT_EDGE",EDGE,{"disambiguationData":[OSD([subQ0,subQ1])]})]});}
            fillet(context, id + "F5", {"entities" : qUnion([Q0, Q1, Q2, Q3]), "radius" : 6 * mm, "tangentPropagation" : true, "allowEdgeOverflow" : false});
        }
        {
            var Q0;
            Q0=makeQuery(id+"F1.opExtrude","CAP_EDGE",EDGE,{"disambiguationData":[OSD([sQuery(id+"F0.wireOp",EDGE,"E0.right")])],"isStart":false});
            chamfer(context, id + "F6", {"entities" : qUnion([Q0]), "chamferType" : ChamferType.OFFSET_ANGLE, "width" : 1 * mm, "oppositeDirection" : false, "angle" : 60 * degree, "tangentPropagation" : true});
        }
        {
            var Q0;
            Q0=qCreatedBy(makeId("Top.planeOp"),FACE);
            var sketch = newSketch(context, id + "F7", { "sketchPlane" : qUnion([Q0])});
            skLineSegment(sketch, "E74.bottom", {"start": v(-90.8, -49.72) * mm, "end": v(-38.9, -49.72) * mm});
            skLineSegment(sketch, "E74.top", {"start": v(-90.8, -21.45) * mm, "end": v(-38.9, -21.45) * mm});
            skLineSegment(sketch, "E74.left", {"start": v(-90.8, -49.72) * mm, "end": v(-90.8, -21.45) * mm});
            skLineSegment(sketch, "E74.right", {"start": v(-38.9, -49.72) * mm, "end": v(-38.9, -21.45) * mm});
            skSolve(sketch);
        }
        {
            var Q0;
            Q0=makeQuery(id+"F0.imprint","IMPRINT",FACE,{"disambiguationData":[TD([[makeQuery(id+"F0.imprint","IMPRINT",EDGE,{"derivedFrom":sQuery(id+"F0.wireOp",EDGE,"E48")}),1.0]])]});
            var Q1;
            Q1=makeQuery(id+"F0.imprint","IMPRINT",FACE,{"disambiguationData":[TD([[makeQuery(id+"F0.imprint","IMPRINT",EDGE,{"derivedFrom":sQuery(id+"F0.wireOp",EDGE,"E50")}),1.0]])]});
            var Q2;
            Q2=makeQuery(id+"F0.imprint","IMPRINT",FACE,{"disambiguationData":[TD([[makeQuery(id+"F0.imprint","IMPRINT",EDGE,{"derivedFrom":sQuery(id+"F0.wireOp",EDGE,"E35.rect.bottom")}),-1.0]])]});
            var Q3;
            Q3=makeQuery(id+"F0.imprint","IMPRINT",FACE,{"disambiguationData":[TD([[makeQuery(id+"F0.imprint","IMPRINT",EDGE,{"derivedFrom":sQuery(id+"F0.wireOp",EDGE,"E32.rect.top")}),-1.0]])]});
            var Q4;
            Q4=makeQuery(id+"F0.imprint","IMPRINT",FACE,{"disambiguationData":[TD([[makeQuery(id+"F0.imprint","IMPRINT",EDGE,{"derivedFrom":sQuery(id+"F0.wireOp",EDGE,"E49")}),1.0]])]});
            var Q5;
            Q5=makeQuery(id+"F0.imprint","IMPRINT",FACE,{"disambiguationData":[TD([[makeQuery(id+"F0.imprint","IMPRINT",EDGE,{"derivedFrom":sQuery(id+"F0.wireOp",EDGE,"E46")}),1.0]])]});
            var Q6;
            Q6=makeQuery(id+"F0.imprint","IMPRINT",FACE,{"disambiguationData":[TD([[makeQuery(id+"F0.imprint","IMPRINT",EDGE,{"derivedFrom":sQuery(id+"F0.wireOp",EDGE,"E45")}),1.0]])]});
            var Q7;
            Q7=makeQuery(id+"F0.imprint","IMPRINT",FACE,{"disambiguationData":[TD([[makeQuery(id+"F0.imprint","IMPRINT",EDGE,{"derivedFrom":sQuery(id+"F0.wireOp",EDGE,"E47")}),1.0]])]});
            extrude(context, id + "F8", {"entities" : qUnion([Q0, Q1, Q2, Q3, Q4, Q5, Q6, Q7]), "operationType" : NewBodyOperationType.ADD, "depth" : 8.25 * mm});
        }
    });
